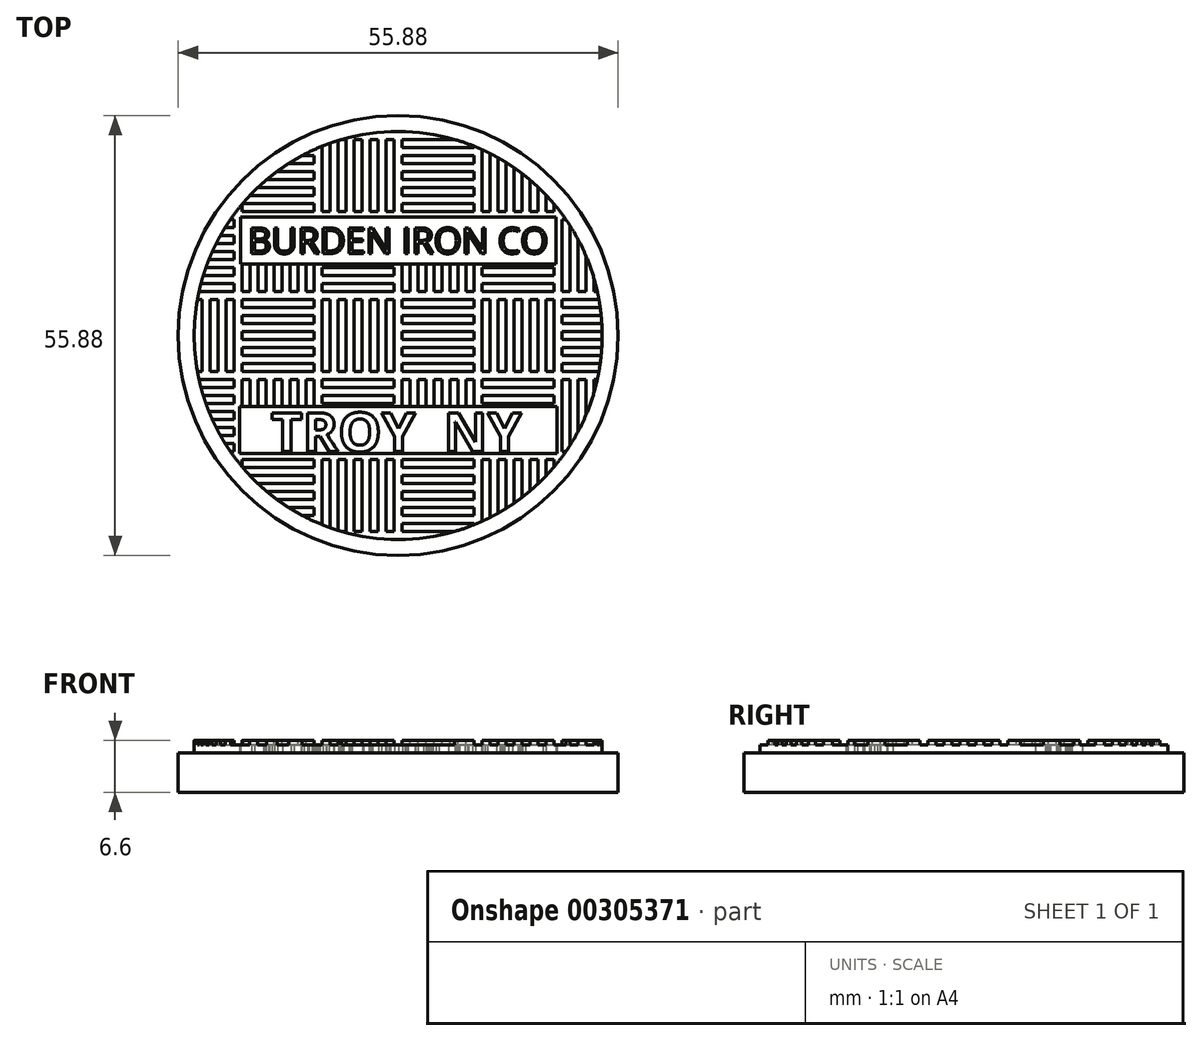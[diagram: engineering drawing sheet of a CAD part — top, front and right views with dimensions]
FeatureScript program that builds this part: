
annotation { "Feature Type Name" : "Feature", "Feature Type Description" : "" }
export const myFeature = defineFeature(function(context is Context, id is Id, definition is map)
    precondition{}
    {
        {
            var Q0;
            Q0=qCreatedBy(makeId("Top.planeOp"),FACE);
            var sketch = newSketch(context, id + "F0", { "sketchPlane" : qUnion([Q0])});
            skCircle(sketch, "E0", {"center": v(0, 0) * mm, "radius": 27.94 * mm});
            skSolve(sketch);
        }
        {
            var Q0;
            Q0 = qSketchRegion(id + "F0", true);
            extrude(context, id + "F1", {"entities" : qUnion([Q0]), "depth" : 6 * mm});
        }
        {
            var Q0;
            Q0=makeQuery(id+"F1.opExtrude","CAP_FACE",FACE,{"disambiguationData":[OSD([sQuery(id+"F0.wireOp",EDGE,"E0")])],"isStart":false});
            var sketch = newSketch(context, id + "F2", { "sketchPlane" : qUnion([Q0])});
            skLineSegment(sketch, "E1.bottom", {"start": v(-9.65, 4.57) * mm, "end": v(-8.64, 4.57) * mm});
            skLineSegment(sketch, "E1.top", {"start": v(-9.65, -4.57) * mm, "end": v(-8.64, -4.57) * mm});
            skLineSegment(sketch, "E1.left", {"start": v(-9.65, 4.57) * mm, "end": v(-9.65, -4.57) * mm});
            skLineSegment(sketch, "E1.right", {"start": v(-8.64, 4.57) * mm, "end": v(-8.64, -4.57) * mm});
            skPoint(sketch, "E2", {"position": v(-9.65, 0) * mm});
            skLineSegment(sketch, "E3.1.0.0", {"start": v(-7.62, 4.57) * mm, "end": v(-7.62, -4.57) * mm});
            skLineSegment(sketch, "E3.1.0.1", {"start": v(-7.62, 4.57) * mm, "end": v(-6.6, 4.57) * mm});
            skLineSegment(sketch, "E3.1.0.2", {"start": v(-6.6, 4.57) * mm, "end": v(-6.6, -4.57) * mm});
            skLineSegment(sketch, "E3.1.0.3", {"start": v(-7.62, -4.57) * mm, "end": v(-6.6, -4.57) * mm});
            skLineSegment(sketch, "E3.2.0.0", {"start": v(-5.59, 4.57) * mm, "end": v(-5.59, -4.57) * mm});
            skLineSegment(sketch, "E3.2.0.1", {"start": v(-5.59, 4.57) * mm, "end": v(-4.57, 4.57) * mm});
            skLineSegment(sketch, "E3.2.0.2", {"start": v(-4.57, 4.57) * mm, "end": v(-4.57, -4.57) * mm});
            skLineSegment(sketch, "E3.2.0.3", {"start": v(-5.59, -4.57) * mm, "end": v(-4.57, -4.57) * mm});
            skLineSegment(sketch, "E3.3.0.0", {"start": v(-3.56, 4.57) * mm, "end": v(-3.56, -4.57) * mm});
            skLineSegment(sketch, "E3.3.0.1", {"start": v(-3.56, 4.57) * mm, "end": v(-2.54, 4.57) * mm});
            skLineSegment(sketch, "E3.3.0.2", {"start": v(-2.54, 4.57) * mm, "end": v(-2.54, -4.57) * mm});
            skLineSegment(sketch, "E3.3.0.3", {"start": v(-3.56, -4.57) * mm, "end": v(-2.54, -4.57) * mm});
            skLineSegment(sketch, "E3.4.0.0", {"start": v(-1.52, 4.57) * mm, "end": v(-1.52, -4.57) * mm});
            skLineSegment(sketch, "E3.4.0.1", {"start": v(-1.52, 4.57) * mm, "end": v(-0.5, 4.57) * mm});
            skLineSegment(sketch, "E3.4.0.2", {"start": v(-0.5, 4.57) * mm, "end": v(-0.5, -4.57) * mm});
            skLineSegment(sketch, "E3.4.0.3", {"start": v(-1.52, -4.57) * mm, "end": v(-0.5, -4.57) * mm});
            skLineSegment(sketch, "E3.direction1", {"start": v(-9.65, -4.57) * mm, "end": v(-7.62, -4.57) * mm, "construction": true});
            skLineSegment(sketch, "E4.bottom", {"start": v(0.5, 4.57) * mm, "end": v(9.65, 4.57) * mm});
            skLineSegment(sketch, "E4.top", {"start": v(0.5, 3.56) * mm, "end": v(9.65, 3.56) * mm});
            skLineSegment(sketch, "E4.left", {"start": v(0.5, 4.57) * mm, "end": v(0.5, 3.56) * mm});
            skLineSegment(sketch, "E4.right", {"start": v(9.65, 4.57) * mm, "end": v(9.65, 3.56) * mm});
            skLineSegment(sketch, "E5.bottom", {"start": v(0.5, 2.54) * mm, "end": v(9.65, 2.54) * mm});
            skLineSegment(sketch, "E5.top", {"start": v(0.5, 1.52) * mm, "end": v(9.65, 1.52) * mm});
            skLineSegment(sketch, "E5.left", {"start": v(0.5, 2.54) * mm, "end": v(0.5, 1.52) * mm});
            skLineSegment(sketch, "E5.right", {"start": v(9.65, 2.54) * mm, "end": v(9.65, 1.52) * mm});
            skPoint(sketch, "E6.firstSnap0", {"position": v(0.5, 2.03) * mm});
            skPoint(sketch, "E6.oppositeSnap0", {"position": v(9.65, 2.03) * mm});
            skLineSegment(sketch, "E6.bottom", {"start": v(0.5, 0.5) * mm, "end": v(9.65, 0.5) * mm});
            skLineSegment(sketch, "E6.top", {"start": v(0.5, -0.5) * mm, "end": v(9.65, -0.5) * mm});
            skLineSegment(sketch, "E6.left", {"start": v(0.5, 0.5) * mm, "end": v(0.5, -0.5) * mm});
            skLineSegment(sketch, "E6.right", {"start": v(9.65, 0.5) * mm, "end": v(9.65, -0.5) * mm});
            skLineSegment(sketch, "E7.bottom", {"start": v(0.5, -1.52) * mm, "end": v(9.65, -1.52) * mm});
            skLineSegment(sketch, "E7.top", {"start": v(0.5, -2.54) * mm, "end": v(9.65, -2.54) * mm});
            skLineSegment(sketch, "E7.left", {"start": v(0.5, -1.52) * mm, "end": v(0.5, -2.54) * mm});
            skLineSegment(sketch, "E7.right", {"start": v(9.65, -1.52) * mm, "end": v(9.65, -2.54) * mm});
            skPoint(sketch, "E8.oppositeSnap0", {"position": v(9.65, -2.03) * mm});
            skLineSegment(sketch, "E8.bottom", {"start": v(0.5, -3.56) * mm, "end": v(9.65, -3.56) * mm});
            skLineSegment(sketch, "E8.top", {"start": v(0.5, -4.57) * mm, "end": v(9.65, -4.57) * mm});
            skLineSegment(sketch, "E8.left", {"start": v(0.5, -3.56) * mm, "end": v(0.5, -4.57) * mm});
            skLineSegment(sketch, "E8.right", {"start": v(9.65, -3.56) * mm, "end": v(9.65, -4.57) * mm});
            skLineSegment(sketch, "E9.bottom", {"start": v(-9.65, 14.73) * mm, "end": v(-0.5, 14.73) * mm});
            skLineSegment(sketch, "E9.top", {"start": v(-9.65, 13.72) * mm, "end": v(-0.5, 13.72) * mm});
            skLineSegment(sketch, "E9.left", {"start": v(-9.65, 14.73) * mm, "end": v(-9.65, 13.72) * mm});
            skLineSegment(sketch, "E9.right", {"start": v(-0.5, 14.73) * mm, "end": v(-0.5, 13.72) * mm});
            skLineSegment(sketch, "E10.bottom", {"start": v(-9.65, 12.7) * mm, "end": v(-0.5, 12.7) * mm});
            skLineSegment(sketch, "E10.top", {"start": v(-9.65, 11.68) * mm, "end": v(-0.5, 11.68) * mm});
            skLineSegment(sketch, "E10.left", {"start": v(-9.65, 12.7) * mm, "end": v(-9.65, 11.68) * mm});
            skLineSegment(sketch, "E10.right", {"start": v(-0.5, 12.7) * mm, "end": v(-0.5, 11.68) * mm});
            skPoint(sketch, "E11.firstSnap0", {"position": v(-9.65, 12.2) * mm});
            skPoint(sketch, "E11.oppositeSnap0", {"position": v(-0.5, 12.2) * mm});
            skLineSegment(sketch, "E11.bottom", {"start": v(-9.65, 10.67) * mm, "end": v(-0.5, 10.67) * mm});
            skLineSegment(sketch, "E11.top", {"start": v(-9.65, 9.65) * mm, "end": v(-0.5, 9.65) * mm});
            skLineSegment(sketch, "E11.left", {"start": v(-9.65, 10.67) * mm, "end": v(-9.65, 9.65) * mm});
            skLineSegment(sketch, "E11.right", {"start": v(-0.5, 10.67) * mm, "end": v(-0.5, 9.65) * mm});
            skLineSegment(sketch, "E12.bottom", {"start": v(-9.65, 8.64) * mm, "end": v(-0.5, 8.64) * mm});
            skLineSegment(sketch, "E12.top", {"start": v(-9.65, 7.62) * mm, "end": v(-0.5, 7.62) * mm});
            skLineSegment(sketch, "E12.left", {"start": v(-9.65, 8.64) * mm, "end": v(-9.65, 7.62) * mm});
            skLineSegment(sketch, "E12.right", {"start": v(-0.5, 8.64) * mm, "end": v(-0.5, 7.62) * mm});
            skPoint(sketch, "E13.oppositeSnap0", {"position": v(-0.5, 8.13) * mm});
            skLineSegment(sketch, "E13.bottom", {"start": v(-9.65, 6.6) * mm, "end": v(-0.5, 6.6) * mm});
            skLineSegment(sketch, "E13.top", {"start": v(-9.65, 5.59) * mm, "end": v(-0.5, 5.59) * mm});
            skLineSegment(sketch, "E13.left", {"start": v(-9.65, 6.6) * mm, "end": v(-9.65, 5.59) * mm});
            skLineSegment(sketch, "E13.right", {"start": v(-0.5, 6.6) * mm, "end": v(-0.5, 5.59) * mm});
            skLineSegment(sketch, "E14.bottom", {"start": v(0.5, 14.73) * mm, "end": v(1.52, 14.73) * mm});
            skLineSegment(sketch, "E14.top", {"start": v(0.5, 5.59) * mm, "end": v(1.52, 5.59) * mm});
            skLineSegment(sketch, "E14.left", {"start": v(0.5, 14.73) * mm, "end": v(0.5, 5.59) * mm});
            skLineSegment(sketch, "E14.right", {"start": v(1.52, 14.73) * mm, "end": v(1.52, 5.59) * mm});
            skPoint(sketch, "E15", {"position": v(0.5, 10.16) * mm});
            skLineSegment(sketch, "E16.1.0.0", {"start": v(2.54, 14.73) * mm, "end": v(2.54, 5.59) * mm});
            skLineSegment(sketch, "E16.1.0.1", {"start": v(2.54, 14.73) * mm, "end": v(3.56, 14.73) * mm});
            skLineSegment(sketch, "E16.1.0.2", {"start": v(3.56, 14.73) * mm, "end": v(3.56, 5.59) * mm});
            skLineSegment(sketch, "E16.1.0.3", {"start": v(2.54, 5.59) * mm, "end": v(3.56, 5.59) * mm});
            skLineSegment(sketch, "E16.2.0.0", {"start": v(4.57, 14.73) * mm, "end": v(4.57, 5.59) * mm});
            skLineSegment(sketch, "E16.2.0.1", {"start": v(4.57, 14.73) * mm, "end": v(5.59, 14.73) * mm});
            skLineSegment(sketch, "E16.2.0.2", {"start": v(5.59, 14.73) * mm, "end": v(5.59, 5.59) * mm});
            skLineSegment(sketch, "E16.2.0.3", {"start": v(4.57, 5.59) * mm, "end": v(5.59, 5.59) * mm});
            skLineSegment(sketch, "E16.3.0.0", {"start": v(6.6, 14.73) * mm, "end": v(6.6, 5.59) * mm});
            skLineSegment(sketch, "E16.3.0.1", {"start": v(6.6, 14.73) * mm, "end": v(7.62, 14.73) * mm});
            skLineSegment(sketch, "E16.3.0.2", {"start": v(7.62, 14.73) * mm, "end": v(7.62, 5.59) * mm});
            skLineSegment(sketch, "E16.3.0.3", {"start": v(6.6, 5.59) * mm, "end": v(7.62, 5.59) * mm});
            skLineSegment(sketch, "E16.4.0.0", {"start": v(8.64, 14.73) * mm, "end": v(8.64, 5.59) * mm});
            skLineSegment(sketch, "E16.4.0.1", {"start": v(8.64, 14.73) * mm, "end": v(9.65, 14.73) * mm});
            skLineSegment(sketch, "E16.4.0.2", {"start": v(9.65, 14.73) * mm, "end": v(9.65, 5.59) * mm});
            skLineSegment(sketch, "E16.4.0.3", {"start": v(8.64, 5.59) * mm, "end": v(9.65, 5.59) * mm});
            skLineSegment(sketch, "E16.direction1", {"start": v(0.5, 5.59) * mm, "end": v(2.54, 5.59) * mm, "construction": true});
            skLineSegment(sketch, "E17.1.0.0", {"start": v(20.83, -1.52) * mm, "end": v(29.97, -1.52) * mm});
            skLineSegment(sketch, "E17.1.0.1", {"start": v(10.67, 14.73) * mm, "end": v(19.81, 14.73) * mm});
            skLineSegment(sketch, "E17.1.0.2", {"start": v(10.67, 9.65) * mm, "end": v(19.81, 9.65) * mm});
            skPoint(sketch, "E17.1.0.3", {"position": v(10.67, 0) * mm});
            skLineSegment(sketch, "E17.1.0.4", {"start": v(19.81, 4.57) * mm, "end": v(19.81, -4.57) * mm});
            skPoint(sketch, "E17.1.0.5", {"position": v(10.67, 12.2) * mm});
            skLineSegment(sketch, "E17.1.0.6", {"start": v(10.67, 5.59) * mm, "end": v(19.81, 5.59) * mm});
            skLineSegment(sketch, "E17.1.0.7", {"start": v(16.76, 4.57) * mm, "end": v(16.76, -4.57) * mm});
            skLineSegment(sketch, "E17.1.0.8", {"start": v(23.88, 14.73) * mm, "end": v(23.88, 5.59) * mm});
            skLineSegment(sketch, "E17.1.0.9", {"start": v(10.67, 12.7) * mm, "end": v(19.81, 12.7) * mm});
            skLineSegment(sketch, "E17.1.0.10", {"start": v(25.9, 14.73) * mm, "end": v(25.9, 5.59) * mm});
            skLineSegment(sketch, "E17.1.0.11", {"start": v(21.84, 14.73) * mm, "end": v(21.84, 5.59) * mm});
            skLineSegment(sketch, "E17.1.0.12", {"start": v(22.86, 14.73) * mm, "end": v(22.86, 5.59) * mm});
            skLineSegment(sketch, "E17.1.0.13", {"start": v(20.83, -2.54) * mm, "end": v(29.97, -2.54) * mm});
            skLineSegment(sketch, "E17.1.0.14", {"start": v(10.67, 6.6) * mm, "end": v(19.81, 6.6) * mm});
            skLineSegment(sketch, "E17.1.0.15", {"start": v(26.92, 14.73) * mm, "end": v(26.92, 5.59) * mm});
            skLineSegment(sketch, "E17.1.0.16", {"start": v(10.67, 13.72) * mm, "end": v(19.81, 13.72) * mm});
            skLineSegment(sketch, "E17.1.0.17", {"start": v(20.83, 1.52) * mm, "end": v(29.97, 1.52) * mm});
            skLineSegment(sketch, "E17.1.0.18", {"start": v(24.9, 14.73) * mm, "end": v(24.9, 5.59) * mm});
            skLineSegment(sketch, "E17.1.0.19", {"start": v(10.67, 8.64) * mm, "end": v(19.81, 8.64) * mm});
            skLineSegment(sketch, "E17.1.0.20", {"start": v(10.67, 11.68) * mm, "end": v(19.81, 11.68) * mm});
            skPoint(sketch, "E17.1.0.21", {"position": v(20.83, 10.16) * mm});
            skLineSegment(sketch, "E17.1.0.22", {"start": v(17.78, 4.57) * mm, "end": v(17.78, -4.57) * mm});
            skLineSegment(sketch, "E17.1.0.23", {"start": v(20.83, 0.5) * mm, "end": v(29.97, 0.5) * mm});
            skLineSegment(sketch, "E17.1.0.24", {"start": v(20.83, -4.57) * mm, "end": v(29.97, -4.57) * mm});
            skLineSegment(sketch, "E17.1.0.25", {"start": v(10.67, 10.67) * mm, "end": v(19.81, 10.67) * mm});
            skLineSegment(sketch, "E17.1.0.26", {"start": v(29.97, 14.73) * mm, "end": v(29.97, 5.59) * mm});
            skLineSegment(sketch, "E17.1.0.27", {"start": v(10.67, 7.62) * mm, "end": v(19.81, 7.62) * mm});
            skLineSegment(sketch, "E17.1.0.28", {"start": v(18.8, 4.57) * mm, "end": v(18.8, -4.57) * mm});
            skLineSegment(sketch, "E17.1.0.29", {"start": v(15.75, 4.57) * mm, "end": v(15.75, -4.57) * mm});
            skLineSegment(sketch, "E17.1.0.30", {"start": v(14.73, 4.57) * mm, "end": v(14.73, -4.57) * mm});
            skLineSegment(sketch, "E17.1.0.31", {"start": v(13.72, 4.57) * mm, "end": v(13.72, -4.57) * mm});
            skLineSegment(sketch, "E17.1.0.32", {"start": v(28.96, 14.73) * mm, "end": v(28.96, 5.59) * mm});
            skLineSegment(sketch, "E17.1.0.33", {"start": v(12.7, 4.57) * mm, "end": v(12.7, -4.57) * mm});
            skLineSegment(sketch, "E17.1.0.34", {"start": v(11.68, 4.57) * mm, "end": v(11.68, -4.57) * mm});
            skLineSegment(sketch, "E17.1.0.35", {"start": v(10.67, 4.57) * mm, "end": v(10.67, -4.57) * mm});
            skLineSegment(sketch, "E17.1.0.36", {"start": v(20.83, -0.5) * mm, "end": v(29.97, -0.5) * mm});
            skLineSegment(sketch, "E17.1.0.37", {"start": v(20.83, -3.56) * mm, "end": v(29.97, -3.56) * mm});
            skLineSegment(sketch, "E17.1.0.38", {"start": v(27.94, 14.73) * mm, "end": v(27.94, 5.59) * mm});
            skPoint(sketch, "E17.1.0.39", {"position": v(19.81, 12.2) * mm});
            skLineSegment(sketch, "E17.1.0.40", {"start": v(20.83, 2.54) * mm, "end": v(29.97, 2.54) * mm});
            skPoint(sketch, "E17.1.0.41", {"position": v(19.81, 8.13) * mm});
            skPoint(sketch, "E17.1.0.42", {"position": v(29.97, -2.03) * mm});
            skPoint(sketch, "E17.1.0.43", {"position": v(29.97, 2.03) * mm});
            skLineSegment(sketch, "E17.1.0.44", {"start": v(20.83, 14.73) * mm, "end": v(20.83, 5.59) * mm});
            skLineSegment(sketch, "E17.1.0.45", {"start": v(20.83, 3.56) * mm, "end": v(29.97, 3.56) * mm});
            skLineSegment(sketch, "E17.1.0.46", {"start": v(20.83, 4.57) * mm, "end": v(29.97, 4.57) * mm});
            skPoint(sketch, "E17.1.0.47", {"position": v(20.83, 2.03) * mm});
            skLineSegment(sketch, "E17.1.0.48", {"start": v(10.67, 10.67) * mm, "end": v(10.67, 9.65) * mm});
            skLineSegment(sketch, "E17.1.0.49", {"start": v(18.8, 4.57) * mm, "end": v(19.81, 4.57) * mm});
            skLineSegment(sketch, "E17.1.0.50", {"start": v(10.67, -4.57) * mm, "end": v(12.7, -4.57) * mm, "construction": true});
            skLineSegment(sketch, "E17.1.0.51", {"start": v(18.8, -4.57) * mm, "end": v(19.81, -4.57) * mm});
            skLineSegment(sketch, "E17.1.0.52", {"start": v(28.96, 5.59) * mm, "end": v(29.97, 5.59) * mm});
            skLineSegment(sketch, "E17.1.0.53", {"start": v(26.92, 14.73) * mm, "end": v(27.94, 14.73) * mm});
            skLineSegment(sketch, "E17.1.0.54", {"start": v(20.83, 5.59) * mm, "end": v(22.86, 5.59) * mm, "construction": true});
            skLineSegment(sketch, "E17.1.0.55", {"start": v(22.86, 14.73) * mm, "end": v(23.88, 14.73) * mm});
            skLineSegment(sketch, "E17.1.0.56", {"start": v(20.83, -3.56) * mm, "end": v(20.83, -4.57) * mm});
            skLineSegment(sketch, "E17.1.0.57", {"start": v(10.67, 8.64) * mm, "end": v(10.67, 7.62) * mm});
            skLineSegment(sketch, "E17.1.0.58", {"start": v(14.73, -4.57) * mm, "end": v(15.75, -4.57) * mm});
            skLineSegment(sketch, "E17.1.0.59", {"start": v(10.67, 14.73) * mm, "end": v(10.67, 13.72) * mm});
            skLineSegment(sketch, "E17.1.0.60", {"start": v(20.83, -1.52) * mm, "end": v(20.83, -2.54) * mm});
            skLineSegment(sketch, "E17.1.0.61", {"start": v(28.96, 14.73) * mm, "end": v(29.97, 14.73) * mm});
            skLineSegment(sketch, "E17.1.0.62", {"start": v(20.83, 5.59) * mm, "end": v(21.84, 5.59) * mm});
            skLineSegment(sketch, "E17.1.0.63", {"start": v(16.76, -4.57) * mm, "end": v(17.78, -4.57) * mm});
            skLineSegment(sketch, "E17.1.0.64", {"start": v(20.83, 0.5) * mm, "end": v(20.83, -0.5) * mm});
            skLineSegment(sketch, "E17.1.0.65", {"start": v(24.9, 14.73) * mm, "end": v(25.9, 14.73) * mm});
            skLineSegment(sketch, "E17.1.0.66", {"start": v(29.97, -3.56) * mm, "end": v(29.97, -4.57) * mm});
            skLineSegment(sketch, "E17.1.0.67", {"start": v(12.7, -4.57) * mm, "end": v(13.72, -4.57) * mm});
            skLineSegment(sketch, "E17.1.0.68", {"start": v(12.7, 4.57) * mm, "end": v(13.72, 4.57) * mm});
            skLineSegment(sketch, "E17.1.0.69", {"start": v(20.83, 14.73) * mm, "end": v(21.84, 14.73) * mm});
            skLineSegment(sketch, "E17.1.0.70", {"start": v(20.83, 4.57) * mm, "end": v(20.83, 3.56) * mm});
            skLineSegment(sketch, "E17.1.0.71", {"start": v(10.67, -4.57) * mm, "end": v(11.68, -4.57) * mm});
            skLineSegment(sketch, "E17.1.0.72", {"start": v(10.67, 4.57) * mm, "end": v(11.68, 4.57) * mm});
            skLineSegment(sketch, "E17.1.0.73", {"start": v(19.81, 14.73) * mm, "end": v(19.81, 13.72) * mm});
            skLineSegment(sketch, "E17.1.0.74", {"start": v(10.67, 6.6) * mm, "end": v(10.67, 5.59) * mm});
            skLineSegment(sketch, "E17.1.0.75", {"start": v(19.81, 8.64) * mm, "end": v(19.81, 7.62) * mm});
            skLineSegment(sketch, "E17.1.0.76", {"start": v(19.81, 12.7) * mm, "end": v(19.81, 11.68) * mm});
            skLineSegment(sketch, "E17.1.0.77", {"start": v(24.9, 5.59) * mm, "end": v(25.9, 5.59) * mm});
            skLineSegment(sketch, "E17.1.0.78", {"start": v(22.86, 5.59) * mm, "end": v(23.88, 5.59) * mm});
            skLineSegment(sketch, "E17.1.0.79", {"start": v(10.67, 12.7) * mm, "end": v(10.67, 11.68) * mm});
            skLineSegment(sketch, "E17.1.0.80", {"start": v(20.83, 2.54) * mm, "end": v(20.83, 1.52) * mm});
            skLineSegment(sketch, "E17.1.0.81", {"start": v(19.81, 10.67) * mm, "end": v(19.81, 9.65) * mm});
            skLineSegment(sketch, "E17.1.0.82", {"start": v(29.97, -1.52) * mm, "end": v(29.97, -2.54) * mm});
            skLineSegment(sketch, "E17.1.0.83", {"start": v(16.76, 4.57) * mm, "end": v(17.78, 4.57) * mm});
            skLineSegment(sketch, "E17.1.0.84", {"start": v(29.97, 4.57) * mm, "end": v(29.97, 3.56) * mm});
            skLineSegment(sketch, "E17.1.0.85", {"start": v(29.97, 0.5) * mm, "end": v(29.97, -0.5) * mm});
            skLineSegment(sketch, "E17.1.0.86", {"start": v(14.73, 4.57) * mm, "end": v(15.75, 4.57) * mm});
            skLineSegment(sketch, "E17.1.0.87", {"start": v(19.81, 6.6) * mm, "end": v(19.81, 5.59) * mm});
            skLineSegment(sketch, "E17.1.0.88", {"start": v(26.92, 5.59) * mm, "end": v(27.94, 5.59) * mm});
            skLineSegment(sketch, "E17.1.0.89", {"start": v(29.97, 2.54) * mm, "end": v(29.97, 1.52) * mm});
            skLineSegment(sketch, "E17.direction1", {"start": v(-9.65, -4.57) * mm, "end": v(10.67, -4.57) * mm, "construction": true});
            skLineSegment(sketch, "E18.1.0.0", {"start": v(-29.97, 8.64) * mm, "end": v(-20.83, 8.64) * mm});
            skLineSegment(sketch, "E18.1.0.1", {"start": v(-15.75, 14.73) * mm, "end": v(-15.75, 5.59) * mm});
            skLineSegment(sketch, "E18.1.0.2", {"start": v(-19.81, 4.57) * mm, "end": v(-10.67, 4.57) * mm});
            skLineSegment(sketch, "E18.1.0.3", {"start": v(-19.81, -3.56) * mm, "end": v(-10.67, -3.56) * mm});
            skLineSegment(sketch, "E18.1.0.4", {"start": v(-19.81, 1.52) * mm, "end": v(-10.67, 1.52) * mm});
            skLineSegment(sketch, "E18.1.0.5", {"start": v(-29.97, 13.72) * mm, "end": v(-20.83, 13.72) * mm});
            skLineSegment(sketch, "E18.1.0.6", {"start": v(-29.97, 5.59) * mm, "end": v(-20.83, 5.59) * mm});
            skPoint(sketch, "E18.1.0.7", {"position": v(-29.97, 0) * mm});
            skLineSegment(sketch, "E18.1.0.8", {"start": v(-19.81, 2.54) * mm, "end": v(-10.67, 2.54) * mm});
            skLineSegment(sketch, "E18.1.0.9", {"start": v(-29.97, 14.73) * mm, "end": v(-20.83, 14.73) * mm});
            skLineSegment(sketch, "E18.1.0.10", {"start": v(-29.97, 6.6) * mm, "end": v(-20.83, 6.6) * mm});
            skLineSegment(sketch, "E18.1.0.11", {"start": v(-13.72, 14.73) * mm, "end": v(-13.72, 5.59) * mm});
            skLineSegment(sketch, "E18.1.0.12", {"start": v(-16.76, 14.73) * mm, "end": v(-16.76, 5.59) * mm});
            skLineSegment(sketch, "E18.1.0.14", {"start": v(-29.97, 9.65) * mm, "end": v(-20.83, 9.65) * mm});
            skLineSegment(sketch, "E18.1.0.15", {"start": v(-20.83, 4.57) * mm, "end": v(-20.83, -4.57) * mm});
            skLineSegment(sketch, "E18.1.0.16", {"start": v(-19.81, -2.54) * mm, "end": v(-10.67, -2.54) * mm});
            skLineSegment(sketch, "E18.1.0.18", {"start": v(-29.97, 10.67) * mm, "end": v(-20.83, 10.67) * mm});
            skLineSegment(sketch, "E18.1.0.19", {"start": v(-17.78, 14.73) * mm, "end": v(-17.78, 5.59) * mm});
            skLineSegment(sketch, "E18.1.0.20", {"start": v(-19.81, -1.52) * mm, "end": v(-10.67, -1.52) * mm});
            skPoint(sketch, "E18.1.0.21", {"position": v(-19.81, 10.16) * mm});
            skLineSegment(sketch, "E18.1.0.22", {"start": v(-21.84, 4.57) * mm, "end": v(-21.84, -4.57) * mm});
            skLineSegment(sketch, "E18.1.0.23", {"start": v(-18.8, 14.73) * mm, "end": v(-18.8, 5.59) * mm});
            skLineSegment(sketch, "E18.1.0.24", {"start": v(-23.88, 4.57) * mm, "end": v(-23.88, -4.57) * mm});
            skLineSegment(sketch, "E18.1.0.25", {"start": v(-24.9, 4.57) * mm, "end": v(-24.9, -4.57) * mm});
            skLineSegment(sketch, "E18.1.0.26", {"start": v(-25.9, 4.57) * mm, "end": v(-25.9, -4.57) * mm});
            skLineSegment(sketch, "E18.1.0.27", {"start": v(-10.67, 14.73) * mm, "end": v(-10.67, 5.59) * mm});
            skLineSegment(sketch, "E18.1.0.28", {"start": v(-26.92, 4.57) * mm, "end": v(-26.92, -4.57) * mm});
            skLineSegment(sketch, "E18.1.0.29", {"start": v(-27.94, 4.57) * mm, "end": v(-27.94, -4.57) * mm});
            skLineSegment(sketch, "E18.1.0.30", {"start": v(-28.96, 4.57) * mm, "end": v(-28.96, -4.57) * mm});
            skLineSegment(sketch, "E18.1.0.31", {"start": v(-29.97, 4.57) * mm, "end": v(-29.97, -4.57) * mm});
            skLineSegment(sketch, "E18.1.0.32", {"start": v(-22.86, 4.57) * mm, "end": v(-22.86, -4.57) * mm});
            skPoint(sketch, "E18.1.0.33", {"position": v(-10.67, 2.03) * mm});
            skLineSegment(sketch, "E18.1.0.34", {"start": v(-29.97, 11.68) * mm, "end": v(-20.83, 11.68) * mm});
            skLineSegment(sketch, "E18.1.0.35", {"start": v(-14.73, 14.73) * mm, "end": v(-14.73, 5.59) * mm});
            skLineSegment(sketch, "E18.1.0.36", {"start": v(-19.81, -0.5) * mm, "end": v(-10.67, -0.5) * mm});
            skPoint(sketch, "E18.1.0.37", {"position": v(-29.97, 12.2) * mm});
            skLineSegment(sketch, "E18.1.0.38", {"start": v(-29.97, 12.7) * mm, "end": v(-20.83, 12.7) * mm});
            skLineSegment(sketch, "E18.1.0.39", {"start": v(-11.68, 14.73) * mm, "end": v(-11.68, 5.59) * mm});
            skLineSegment(sketch, "E18.1.0.40", {"start": v(-19.81, 0.5) * mm, "end": v(-10.67, 0.5) * mm});
            skLineSegment(sketch, "E18.1.0.41", {"start": v(-12.7, 14.73) * mm, "end": v(-12.7, 5.59) * mm});
            skLineSegment(sketch, "E18.1.0.42", {"start": v(-29.97, 7.62) * mm, "end": v(-20.83, 7.62) * mm});
            skPoint(sketch, "E18.1.0.43", {"position": v(-10.67, -2.03) * mm});
            skLineSegment(sketch, "E18.1.0.44", {"start": v(-19.81, 3.56) * mm, "end": v(-10.67, 3.56) * mm});
            skLineSegment(sketch, "E18.1.0.45", {"start": v(-19.81, -4.57) * mm, "end": v(-10.67, -4.57) * mm});
            skPoint(sketch, "E18.1.0.46", {"position": v(-20.83, 8.13) * mm});
            skLineSegment(sketch, "E18.1.0.47", {"start": v(-19.81, 14.73) * mm, "end": v(-19.81, 5.59) * mm});
            skPoint(sketch, "E18.1.0.48", {"position": v(-20.83, 12.2) * mm});
            skPoint(sketch, "E18.1.0.49", {"position": v(-19.81, 2.03) * mm});
            skLineSegment(sketch, "E18.1.0.50", {"start": v(-13.72, 14.73) * mm, "end": v(-12.7, 14.73) * mm});
            skLineSegment(sketch, "E18.1.0.51", {"start": v(-17.78, 5.59) * mm, "end": v(-16.76, 5.59) * mm});
            skLineSegment(sketch, "E18.1.0.52", {"start": v(-29.97, -4.57) * mm, "end": v(-27.94, -4.57) * mm, "construction": true});
            skLineSegment(sketch, "E18.1.0.53", {"start": v(-10.67, -1.52) * mm, "end": v(-10.67, -2.54) * mm});
            skLineSegment(sketch, "E18.1.0.54", {"start": v(-29.97, 10.67) * mm, "end": v(-29.97, 9.65) * mm});
            skLineSegment(sketch, "E18.1.0.55", {"start": v(-21.84, -4.57) * mm, "end": v(-20.83, -4.57) * mm});
            skLineSegment(sketch, "E18.1.0.56", {"start": v(-19.81, -1.52) * mm, "end": v(-19.81, -2.54) * mm});
            skLineSegment(sketch, "E18.1.0.57", {"start": v(-17.78, 14.73) * mm, "end": v(-16.76, 14.73) * mm});
            skLineSegment(sketch, "E18.1.0.58", {"start": v(-10.67, 4.57) * mm, "end": v(-10.67, 3.56) * mm});
            skLineSegment(sketch, "E18.1.0.59", {"start": v(-10.67, -3.56) * mm, "end": v(-10.67, -4.57) * mm});
            skLineSegment(sketch, "E18.1.0.60", {"start": v(-19.81, 5.59) * mm, "end": v(-17.78, 5.59) * mm, "construction": true});
            skLineSegment(sketch, "E18.1.0.61", {"start": v(-21.84, 4.57) * mm, "end": v(-20.83, 4.57) * mm});
            skLineSegment(sketch, "E18.1.0.62", {"start": v(-10.67, 0.5) * mm, "end": v(-10.67, -0.5) * mm});
            skLineSegment(sketch, "E18.1.0.63", {"start": v(-11.68, 5.59) * mm, "end": v(-10.67, 5.59) * mm});
            skLineSegment(sketch, "E18.1.0.64", {"start": v(-25.9, -4.57) * mm, "end": v(-24.9, -4.57) * mm});
            skLineSegment(sketch, "E18.1.0.65", {"start": v(-29.97, 12.7) * mm, "end": v(-29.97, 11.68) * mm});
            skLineSegment(sketch, "E18.1.0.66", {"start": v(-27.94, -4.57) * mm, "end": v(-26.92, -4.57) * mm});
            skLineSegment(sketch, "E18.1.0.67", {"start": v(-19.81, 0.5) * mm, "end": v(-19.81, -0.5) * mm});
            skLineSegment(sketch, "E18.1.0.68", {"start": v(-27.94, 4.57) * mm, "end": v(-26.92, 4.57) * mm});
            skLineSegment(sketch, "E18.1.0.69", {"start": v(-29.97, -4.57) * mm, "end": v(-28.96, -4.57) * mm});
            skLineSegment(sketch, "E18.1.0.70", {"start": v(-29.97, 4.57) * mm, "end": v(-28.96, 4.57) * mm});
            skLineSegment(sketch, "E18.1.0.71", {"start": v(-23.88, -4.57) * mm, "end": v(-22.86, -4.57) * mm});
            skLineSegment(sketch, "E18.1.0.72", {"start": v(-19.81, 5.59) * mm, "end": v(-18.8, 5.59) * mm});
            skLineSegment(sketch, "E18.1.0.73", {"start": v(-11.68, 14.73) * mm, "end": v(-10.67, 14.73) * mm});
            skLineSegment(sketch, "E18.1.0.74", {"start": v(-19.81, 4.57) * mm, "end": v(-19.81, 3.56) * mm});
            skLineSegment(sketch, "E18.1.0.75", {"start": v(-19.81, -3.56) * mm, "end": v(-19.81, -4.57) * mm});
            skLineSegment(sketch, "E18.1.0.76", {"start": v(-29.97, 8.64) * mm, "end": v(-29.97, 7.62) * mm});
            skLineSegment(sketch, "E18.1.0.77", {"start": v(-10.67, 2.54) * mm, "end": v(-10.67, 1.52) * mm});
            skLineSegment(sketch, "E18.1.0.78", {"start": v(-20.83, 14.73) * mm, "end": v(-20.83, 13.72) * mm});
            skLineSegment(sketch, "E18.1.0.79", {"start": v(-20.83, 6.6) * mm, "end": v(-20.83, 5.59) * mm});
            skLineSegment(sketch, "E18.1.0.80", {"start": v(-13.72, 5.59) * mm, "end": v(-12.7, 5.59) * mm});
            skLineSegment(sketch, "E18.1.0.81", {"start": v(-19.81, 14.73) * mm, "end": v(-18.8, 14.73) * mm});
            skLineSegment(sketch, "E18.1.0.82", {"start": v(-29.97, 14.73) * mm, "end": v(-29.97, 13.72) * mm});
            skLineSegment(sketch, "E18.1.0.83", {"start": v(-29.97, 6.6) * mm, "end": v(-29.97, 5.59) * mm});
            skLineSegment(sketch, "E18.1.0.84", {"start": v(-15.75, 14.73) * mm, "end": v(-14.73, 14.73) * mm});
            skLineSegment(sketch, "E18.1.0.85", {"start": v(-20.83, 10.67) * mm, "end": v(-20.83, 9.65) * mm});
            skLineSegment(sketch, "E18.1.0.86", {"start": v(-20.83, 8.64) * mm, "end": v(-20.83, 7.62) * mm});
            skLineSegment(sketch, "E18.1.0.87", {"start": v(-15.75, 5.59) * mm, "end": v(-14.73, 5.59) * mm});
            skLineSegment(sketch, "E18.1.0.88", {"start": v(-20.83, 12.7) * mm, "end": v(-20.83, 11.68) * mm});
            skLineSegment(sketch, "E18.1.0.89", {"start": v(-25.9, 4.57) * mm, "end": v(-24.9, 4.57) * mm});
            skLineSegment(sketch, "E18.1.0.90", {"start": v(-23.88, 4.57) * mm, "end": v(-22.86, 4.57) * mm});
            skLineSegment(sketch, "E18.1.0.91", {"start": v(-19.81, 2.54) * mm, "end": v(-19.81, 1.52) * mm});
            skLineSegment(sketch, "E18.direction1", {"start": v(-9.65, -4.57) * mm, "end": v(-29.97, -4.57) * mm, "construction": true});
            skLineSegment(sketch, "E19.0.1.0", {"start": v(10.67, 28.96) * mm, "end": v(19.81, 28.96) * mm});
            skLineSegment(sketch, "E19.0.1.1", {"start": v(10.67, 35.05) * mm, "end": v(19.81, 35.05) * mm});
            skLineSegment(sketch, "E19.0.1.2", {"start": v(3.56, 35.05) * mm, "end": v(3.56, 25.9) * mm});
            skPoint(sketch, "E19.0.1.3", {"position": v(-19.81, 30.48) * mm});
            skLineSegment(sketch, "E19.0.1.4", {"start": v(20.83, 19.81) * mm, "end": v(29.97, 19.81) * mm});
            skLineSegment(sketch, "E19.0.1.5", {"start": v(-14.73, 35.05) * mm, "end": v(-14.73, 25.9) * mm});
            skLineSegment(sketch, "E19.0.1.6", {"start": v(-19.81, 17.78) * mm, "end": v(-10.67, 17.78) * mm});
            skLineSegment(sketch, "E19.0.1.7", {"start": v(-1.52, 24.9) * mm, "end": v(-1.52, 15.75) * mm});
            skLineSegment(sketch, "E19.0.1.8", {"start": v(-3.56, 24.9) * mm, "end": v(-3.56, 15.75) * mm});
            skLineSegment(sketch, "E19.0.1.9", {"start": v(11.68, 24.9) * mm, "end": v(11.68, 15.75) * mm});
            skLineSegment(sketch, "E19.0.1.10", {"start": v(-22.86, 24.9) * mm, "end": v(-22.86, 15.75) * mm});
            skLineSegment(sketch, "E19.0.1.11", {"start": v(-4.57, 24.9) * mm, "end": v(-4.57, 15.75) * mm});
            skLineSegment(sketch, "E19.0.1.12", {"start": v(-5.59, 24.9) * mm, "end": v(-5.59, 15.75) * mm});
            skLineSegment(sketch, "E19.0.1.13", {"start": v(-6.6, 24.9) * mm, "end": v(-6.6, 15.75) * mm});
            skLineSegment(sketch, "E19.0.1.14", {"start": v(-29.97, 29.97) * mm, "end": v(-20.83, 29.97) * mm});
            skLineSegment(sketch, "E19.0.1.15", {"start": v(-7.62, 24.9) * mm, "end": v(-7.62, 15.75) * mm});
            skLineSegment(sketch, "E19.0.1.16", {"start": v(-8.64, 24.9) * mm, "end": v(-8.64, 15.75) * mm});
            skLineSegment(sketch, "E19.0.1.17", {"start": v(10.67, 32) * mm, "end": v(19.81, 32) * mm});
            skLineSegment(sketch, "E19.0.1.18", {"start": v(-9.65, 24.9) * mm, "end": v(-9.65, 15.75) * mm});
            skPoint(sketch, "E19.0.1.19", {"position": v(-9.65, 32.51) * mm});
            skLineSegment(sketch, "E19.0.1.20", {"start": v(10.67, 29.97) * mm, "end": v(19.81, 29.97) * mm});
            skLineSegment(sketch, "E19.0.1.21", {"start": v(0.5, 18.8) * mm, "end": v(9.65, 18.8) * mm});
            skLineSegment(sketch, "E19.0.1.22", {"start": v(20.83, 21.84) * mm, "end": v(29.97, 21.84) * mm});
            skLineSegment(sketch, "E19.0.1.23", {"start": v(-9.65, 15.75) * mm, "end": v(10.67, 15.75) * mm, "construction": true});
            skLineSegment(sketch, "E19.0.1.24", {"start": v(-2.54, 24.9) * mm, "end": v(-2.54, 15.75) * mm});
            skLineSegment(sketch, "E19.0.1.25", {"start": v(20.83, 16.76) * mm, "end": v(29.97, 16.76) * mm});
            skLineSegment(sketch, "E19.0.1.26", {"start": v(-19.81, 19.81) * mm, "end": v(-10.67, 19.81) * mm});
            skLineSegment(sketch, "E19.0.1.27", {"start": v(-29.97, 30.99) * mm, "end": v(-20.83, 30.99) * mm});
            skLineSegment(sketch, "E19.0.1.28", {"start": v(2.54, 35.05) * mm, "end": v(2.54, 25.9) * mm});
            skLineSegment(sketch, "E19.0.1.29", {"start": v(-9.65, 30.99) * mm, "end": v(-0.5, 30.99) * mm});
            skLineSegment(sketch, "E19.0.1.30", {"start": v(-19.81, 22.86) * mm, "end": v(-10.67, 22.86) * mm});
            skLineSegment(sketch, "E19.0.1.31", {"start": v(-10.67, 35.05) * mm, "end": v(-10.67, 25.9) * mm});
            skLineSegment(sketch, "E19.0.1.32", {"start": v(-19.81, 35.05) * mm, "end": v(-19.81, 25.9) * mm});
            skLineSegment(sketch, "E19.0.1.33", {"start": v(22.86, 35.05) * mm, "end": v(22.86, 25.9) * mm});
            skLineSegment(sketch, "E19.0.1.34", {"start": v(15.75, 24.9) * mm, "end": v(15.75, 15.75) * mm});
            skLineSegment(sketch, "E19.0.1.35", {"start": v(0.5, 16.76) * mm, "end": v(9.65, 16.76) * mm});
            skPoint(sketch, "E19.0.1.36", {"position": v(19.81, 28.45) * mm});
            skLineSegment(sketch, "E19.0.1.37", {"start": v(0.5, 24.9) * mm, "end": v(9.65, 24.9) * mm});
            skLineSegment(sketch, "E19.0.1.38", {"start": v(17.78, 24.9) * mm, "end": v(17.78, 15.75) * mm});
            skLineSegment(sketch, "E19.0.1.39", {"start": v(19.81, 24.9) * mm, "end": v(19.81, 15.75) * mm});
            skLineSegment(sketch, "E19.0.1.40", {"start": v(4.57, 35.05) * mm, "end": v(4.57, 25.9) * mm});
            skLineSegment(sketch, "E19.0.1.41", {"start": v(-9.65, 28.96) * mm, "end": v(-0.5, 28.96) * mm});
            skLineSegment(sketch, "E19.0.1.42", {"start": v(-29.97, 28.96) * mm, "end": v(-20.83, 28.96) * mm});
            skLineSegment(sketch, "E19.0.1.43", {"start": v(27.94, 35.05) * mm, "end": v(27.94, 25.9) * mm});
            skPoint(sketch, "E19.0.1.44", {"position": v(-29.97, 32.51) * mm});
            skLineSegment(sketch, "E19.0.1.45", {"start": v(-29.97, 25.9) * mm, "end": v(-20.83, 25.9) * mm});
            skLineSegment(sketch, "E19.0.1.46", {"start": v(-25.9, 24.9) * mm, "end": v(-25.9, 15.75) * mm});
            skLineSegment(sketch, "E19.0.1.47", {"start": v(21.84, 35.05) * mm, "end": v(21.84, 25.9) * mm});
            skLineSegment(sketch, "E19.0.1.48", {"start": v(-29.97, 33.02) * mm, "end": v(-20.83, 33.02) * mm});
            skLineSegment(sketch, "E19.0.1.49", {"start": v(-17.78, 35.05) * mm, "end": v(-17.78, 25.9) * mm});
            skLineSegment(sketch, "E19.0.1.50", {"start": v(18.8, 24.9) * mm, "end": v(18.8, 15.75) * mm});
            skPoint(sketch, "E19.0.1.51", {"position": v(19.81, 32.51) * mm});
            skLineSegment(sketch, "E19.0.1.52", {"start": v(7.62, 35.05) * mm, "end": v(7.62, 25.9) * mm});
            skLineSegment(sketch, "E19.0.1.53", {"start": v(-29.97, 34.04) * mm, "end": v(-20.83, 34.04) * mm});
            skLineSegment(sketch, "E19.0.1.54", {"start": v(-24.9, 24.9) * mm, "end": v(-24.9, 15.75) * mm});
            skLineSegment(sketch, "E19.0.1.55", {"start": v(25.9, 35.05) * mm, "end": v(25.9, 25.9) * mm});
            skLineSegment(sketch, "E19.0.1.56", {"start": v(-19.81, 23.88) * mm, "end": v(-10.67, 23.88) * mm});
            skLineSegment(sketch, "E19.0.1.57", {"start": v(10.67, 27.94) * mm, "end": v(19.81, 27.94) * mm});
            skPoint(sketch, "E19.0.1.58", {"position": v(20.83, 30.48) * mm});
            skLineSegment(sketch, "E19.0.1.59", {"start": v(0.5, 21.84) * mm, "end": v(9.65, 21.84) * mm});
            skLineSegment(sketch, "E19.0.1.60", {"start": v(-9.65, 34.04) * mm, "end": v(-0.5, 34.04) * mm});
            skLineSegment(sketch, "E19.0.1.61", {"start": v(-9.65, 25.9) * mm, "end": v(-0.5, 25.9) * mm});
            skLineSegment(sketch, "E19.0.1.62", {"start": v(0.5, 23.88) * mm, "end": v(9.65, 23.88) * mm});
            skLineSegment(sketch, "E19.0.1.63", {"start": v(20.83, 20.83) * mm, "end": v(29.97, 20.83) * mm});
            skLineSegment(sketch, "E19.0.1.64", {"start": v(10.67, 25.9) * mm, "end": v(19.81, 25.9) * mm});
            skLineSegment(sketch, "E19.0.1.65", {"start": v(-9.65, 27.94) * mm, "end": v(-0.5, 27.94) * mm});
            skLineSegment(sketch, "E19.0.1.66", {"start": v(-15.75, 35.05) * mm, "end": v(-15.75, 25.9) * mm});
            skPoint(sketch, "E19.0.1.67", {"position": v(-10.67, 18.29) * mm});
            skLineSegment(sketch, "E19.0.1.68", {"start": v(20.83, 22.86) * mm, "end": v(29.97, 22.86) * mm});
            skLineSegment(sketch, "E19.0.1.69", {"start": v(-11.68, 35.05) * mm, "end": v(-11.68, 25.9) * mm});
            skLineSegment(sketch, "E19.0.1.70", {"start": v(-19.81, 18.8) * mm, "end": v(-10.67, 18.8) * mm});
            skLineSegment(sketch, "E19.0.1.71", {"start": v(-19.81, 21.84) * mm, "end": v(-10.67, 21.84) * mm});
            skLineSegment(sketch, "E19.0.1.72", {"start": v(-23.88, 24.9) * mm, "end": v(-23.88, 15.75) * mm});
            skLineSegment(sketch, "E19.0.1.73", {"start": v(-29.97, 27.94) * mm, "end": v(-20.83, 27.94) * mm});
            skLineSegment(sketch, "E19.0.1.74", {"start": v(10.67, 33.02) * mm, "end": v(19.81, 33.02) * mm});
            skPoint(sketch, "E19.0.1.75", {"position": v(10.67, 32.51) * mm});
            skLineSegment(sketch, "E19.0.1.76", {"start": v(29.97, 35.05) * mm, "end": v(29.97, 25.9) * mm});
            skPoint(sketch, "E19.0.1.77", {"position": v(-19.81, 22.35) * mm});
            skLineSegment(sketch, "E19.0.1.78", {"start": v(20.83, 24.9) * mm, "end": v(29.97, 24.9) * mm});
            skLineSegment(sketch, "E19.0.1.79", {"start": v(0.5, 22.86) * mm, "end": v(9.65, 22.86) * mm});
            skLineSegment(sketch, "E19.0.1.80", {"start": v(-9.65, 35.05) * mm, "end": v(-0.5, 35.05) * mm});
            skLineSegment(sketch, "E19.0.1.81", {"start": v(-9.65, 26.92) * mm, "end": v(-0.5, 26.92) * mm});
            skLineSegment(sketch, "E19.0.1.82", {"start": v(6.6, 35.05) * mm, "end": v(6.6, 25.9) * mm});
            skLineSegment(sketch, "E19.0.1.83", {"start": v(0.5, 20.83) * mm, "end": v(9.65, 20.83) * mm});
            skLineSegment(sketch, "E19.0.1.84", {"start": v(20.83, 17.78) * mm, "end": v(29.97, 17.78) * mm});
            skLineSegment(sketch, "E19.0.1.85", {"start": v(5.59, 35.05) * mm, "end": v(5.59, 25.9) * mm});
            skLineSegment(sketch, "E19.0.1.86", {"start": v(8.64, 35.05) * mm, "end": v(8.64, 25.9) * mm});
            skLineSegment(sketch, "E19.0.1.87", {"start": v(-9.65, 33.02) * mm, "end": v(-0.5, 33.02) * mm});
            skPoint(sketch, "E19.0.1.88", {"position": v(29.97, 18.29) * mm});
            skLineSegment(sketch, "E19.0.1.89", {"start": v(14.73, 24.9) * mm, "end": v(14.73, 15.75) * mm});
            skLineSegment(sketch, "E19.0.1.90", {"start": v(-26.92, 24.9) * mm, "end": v(-26.92, 15.75) * mm});
            skLineSegment(sketch, "E19.0.1.91", {"start": v(-29.97, 35.05) * mm, "end": v(-20.83, 35.05) * mm});
            skPoint(sketch, "E19.0.1.92", {"position": v(-20.83, 28.45) * mm});
            skLineSegment(sketch, "E19.0.1.93", {"start": v(20.83, 35.05) * mm, "end": v(20.83, 25.9) * mm});
            skPoint(sketch, "E19.0.1.94", {"position": v(0.5, 30.48) * mm});
            skLineSegment(sketch, "E19.0.1.95", {"start": v(20.83, 15.75) * mm, "end": v(29.97, 15.75) * mm});
            skLineSegment(sketch, "E19.0.1.96", {"start": v(16.76, 24.9) * mm, "end": v(16.76, 15.75) * mm});
            skLineSegment(sketch, "E19.0.1.97", {"start": v(-19.81, 20.83) * mm, "end": v(-10.67, 20.83) * mm});
            skLineSegment(sketch, "E19.0.1.98", {"start": v(-21.84, 24.9) * mm, "end": v(-21.84, 15.75) * mm});
            skLineSegment(sketch, "E19.0.1.99", {"start": v(-19.81, 24.9) * mm, "end": v(-10.67, 24.9) * mm});
            skLineSegment(sketch, "E19.0.1.100", {"start": v(0.5, 19.81) * mm, "end": v(9.65, 19.81) * mm});
            skLineSegment(sketch, "E19.0.1.101", {"start": v(10.67, 26.92) * mm, "end": v(19.81, 26.92) * mm});
            skLineSegment(sketch, "E19.0.1.102", {"start": v(-9.65, 32) * mm, "end": v(-0.5, 32) * mm});
            skLineSegment(sketch, "E19.0.1.103", {"start": v(-9.65, 15.75) * mm, "end": v(-29.97, 15.75) * mm, "construction": true});
            skPoint(sketch, "E19.0.1.104", {"position": v(29.97, 22.35) * mm});
            skLineSegment(sketch, "E19.0.1.105", {"start": v(13.72, 24.9) * mm, "end": v(13.72, 15.75) * mm});
            skLineSegment(sketch, "E19.0.1.106", {"start": v(-27.94, 24.9) * mm, "end": v(-27.94, 15.75) * mm});
            skLineSegment(sketch, "E19.0.1.107", {"start": v(-29.97, 26.92) * mm, "end": v(-20.83, 26.92) * mm});
            skLineSegment(sketch, "E19.0.1.108", {"start": v(-29.97, 32) * mm, "end": v(-20.83, 32) * mm});
            skLineSegment(sketch, "E19.0.1.109", {"start": v(-20.83, 24.9) * mm, "end": v(-20.83, 15.75) * mm});
            skLineSegment(sketch, "E19.0.1.110", {"start": v(0.5, 17.78) * mm, "end": v(9.65, 17.78) * mm});
            skLineSegment(sketch, "E19.0.1.111", {"start": v(-0.5, 24.9) * mm, "end": v(-0.5, 15.75) * mm});
            skLineSegment(sketch, "E19.0.1.112", {"start": v(24.9, 35.05) * mm, "end": v(24.9, 25.9) * mm});
            skLineSegment(sketch, "E19.0.1.113", {"start": v(20.83, 18.8) * mm, "end": v(29.97, 18.8) * mm});
            skLineSegment(sketch, "E19.0.1.114", {"start": v(-9.65, 29.97) * mm, "end": v(-0.5, 29.97) * mm});
            skLineSegment(sketch, "E19.0.1.115", {"start": v(10.67, 24.9) * mm, "end": v(10.67, 15.75) * mm});
            skPoint(sketch, "E19.0.1.116", {"position": v(-9.65, 20.32) * mm});
            skLineSegment(sketch, "E19.0.1.117", {"start": v(26.92, 35.05) * mm, "end": v(26.92, 25.9) * mm});
            skLineSegment(sketch, "E19.0.1.118", {"start": v(9.65, 35.05) * mm, "end": v(9.65, 25.9) * mm});
            skLineSegment(sketch, "E19.0.1.119", {"start": v(0.5, 35.05) * mm, "end": v(0.5, 25.9) * mm});
            skLineSegment(sketch, "E19.0.1.120", {"start": v(28.96, 35.05) * mm, "end": v(28.96, 25.9) * mm});
            skPoint(sketch, "E19.0.1.121", {"position": v(20.83, 22.35) * mm});
            skLineSegment(sketch, "E19.0.1.122", {"start": v(-28.96, 24.9) * mm, "end": v(-28.96, 15.75) * mm});
            skPoint(sketch, "E19.0.1.123", {"position": v(-20.83, 32.51) * mm});
            skLineSegment(sketch, "E19.0.1.124", {"start": v(20.83, 23.88) * mm, "end": v(29.97, 23.88) * mm});
            skPoint(sketch, "E19.0.1.125", {"position": v(10.67, 20.32) * mm});
            skLineSegment(sketch, "E19.0.1.126", {"start": v(-13.72, 35.05) * mm, "end": v(-13.72, 25.9) * mm});
            skLineSegment(sketch, "E19.0.1.127", {"start": v(10.67, 30.99) * mm, "end": v(19.81, 30.99) * mm});
            skLineSegment(sketch, "E19.0.1.128", {"start": v(23.88, 35.05) * mm, "end": v(23.88, 25.9) * mm});
            skLineSegment(sketch, "E19.0.1.129", {"start": v(10.67, 34.04) * mm, "end": v(19.81, 34.04) * mm});
            skLineSegment(sketch, "E19.0.1.130", {"start": v(1.52, 35.05) * mm, "end": v(1.52, 25.9) * mm});
            skLineSegment(sketch, "E19.0.1.131", {"start": v(-12.7, 35.05) * mm, "end": v(-12.7, 25.9) * mm});
            skLineSegment(sketch, "E19.0.1.132", {"start": v(-18.8, 35.05) * mm, "end": v(-18.8, 25.9) * mm});
            skPoint(sketch, "E19.0.1.133", {"position": v(-29.97, 20.32) * mm});
            skLineSegment(sketch, "E19.0.1.134", {"start": v(12.7, 24.9) * mm, "end": v(12.7, 15.75) * mm});
            skLineSegment(sketch, "E19.0.1.135", {"start": v(-29.97, 24.9) * mm, "end": v(-29.97, 15.75) * mm});
            skLineSegment(sketch, "E19.0.1.136", {"start": v(-16.76, 35.05) * mm, "end": v(-16.76, 25.9) * mm});
            skLineSegment(sketch, "E19.0.1.137", {"start": v(-19.81, 16.76) * mm, "end": v(-10.67, 16.76) * mm});
            skPoint(sketch, "E19.0.1.138", {"position": v(9.65, 18.29) * mm});
            skPoint(sketch, "E19.0.1.139", {"position": v(-9.65, 32.51) * mm});
            skPoint(sketch, "E19.0.1.140", {"position": v(0.5, 22.35) * mm});
            skPoint(sketch, "E19.0.1.141", {"position": v(-10.67, 22.35) * mm});
            skPoint(sketch, "E19.0.1.142", {"position": v(-0.5, 32.51) * mm});
            skLineSegment(sketch, "E19.0.1.143", {"start": v(-19.81, 15.75) * mm, "end": v(-10.67, 15.75) * mm});
            skLineSegment(sketch, "E19.0.1.144", {"start": v(0.5, 15.75) * mm, "end": v(9.65, 15.75) * mm});
            skPoint(sketch, "E19.0.1.145", {"position": v(-0.5, 28.45) * mm});
            skPoint(sketch, "E19.0.1.146", {"position": v(9.65, 22.35) * mm});
            skPoint(sketch, "E19.0.1.147", {"position": v(-9.65, 20.32) * mm});
            skLineSegment(sketch, "E19.0.1.148", {"start": v(0.5, 18.8) * mm, "end": v(0.5, 17.78) * mm});
            skLineSegment(sketch, "E19.0.1.149", {"start": v(-1.52, 15.75) * mm, "end": v(-0.5, 15.75) * mm});
            skLineSegment(sketch, "E19.0.1.150", {"start": v(-9.65, 30.99) * mm, "end": v(-9.65, 29.97) * mm});
            skLineSegment(sketch, "E19.0.1.151", {"start": v(29.97, 22.86) * mm, "end": v(29.97, 21.84) * mm});
            skLineSegment(sketch, "E19.0.1.152", {"start": v(19.81, 35.05) * mm, "end": v(19.81, 34.04) * mm});
            skLineSegment(sketch, "E19.0.1.153", {"start": v(10.67, 28.96) * mm, "end": v(10.67, 27.94) * mm});
            skLineSegment(sketch, "E19.0.1.154", {"start": v(-19.81, 25.9) * mm, "end": v(-18.8, 25.9) * mm});
            skLineSegment(sketch, "E19.0.1.155", {"start": v(-19.81, 18.8) * mm, "end": v(-19.81, 17.78) * mm});
            skLineSegment(sketch, "E19.0.1.156", {"start": v(9.65, 20.83) * mm, "end": v(9.65, 19.81) * mm});
            skLineSegment(sketch, "E19.0.1.157", {"start": v(19.81, 26.92) * mm, "end": v(19.81, 25.9) * mm});
            skLineSegment(sketch, "E19.0.1.158", {"start": v(10.67, 15.75) * mm, "end": v(11.68, 15.75) * mm});
            skLineSegment(sketch, "E19.0.1.159", {"start": v(22.86, 35.05) * mm, "end": v(23.88, 35.05) * mm});
            skLineSegment(sketch, "E19.0.1.160", {"start": v(-29.97, 24.9) * mm, "end": v(-28.96, 24.9) * mm});
            skLineSegment(sketch, "E19.0.1.161", {"start": v(-29.97, 30.99) * mm, "end": v(-29.97, 29.97) * mm});
            skLineSegment(sketch, "E19.0.1.162", {"start": v(-5.59, 15.75) * mm, "end": v(-4.57, 15.75) * mm});
            skLineSegment(sketch, "E19.0.1.163", {"start": v(-5.59, 24.9) * mm, "end": v(-4.57, 24.9) * mm});
            skLineSegment(sketch, "E19.0.1.164", {"start": v(-7.62, 15.75) * mm, "end": v(-6.6, 15.75) * mm});
            skLineSegment(sketch, "E19.0.1.165", {"start": v(-20.83, 28.96) * mm, "end": v(-20.83, 27.94) * mm});
            skLineSegment(sketch, "E19.0.1.166", {"start": v(-7.62, 24.9) * mm, "end": v(-6.6, 24.9) * mm});
            skLineSegment(sketch, "E19.0.1.167", {"start": v(-9.65, 15.75) * mm, "end": v(-7.62, 15.75) * mm, "construction": true});
            skLineSegment(sketch, "E19.0.1.168", {"start": v(-1.52, 24.9) * mm, "end": v(-0.5, 24.9) * mm});
            skLineSegment(sketch, "E19.0.1.169", {"start": v(2.54, 25.9) * mm, "end": v(3.56, 25.9) * mm});
            skLineSegment(sketch, "E19.0.1.170", {"start": v(-9.65, 15.75) * mm, "end": v(-8.64, 15.75) * mm});
            skLineSegment(sketch, "E19.0.1.171", {"start": v(-9.65, 24.9) * mm, "end": v(-8.64, 24.9) * mm});
            skLineSegment(sketch, "E19.0.1.172", {"start": v(-3.56, 15.75) * mm, "end": v(-2.54, 15.75) * mm});
            skLineSegment(sketch, "E19.0.1.173", {"start": v(10.67, 26.92) * mm, "end": v(10.67, 25.9) * mm});
            skLineSegment(sketch, "E19.0.1.174", {"start": v(14.73, 15.75) * mm, "end": v(15.75, 15.75) * mm});
            skLineSegment(sketch, "E19.0.1.175", {"start": v(0.5, 25.9) * mm, "end": v(2.54, 25.9) * mm, "construction": true});
            skLineSegment(sketch, "E19.0.1.176", {"start": v(-11.68, 35.05) * mm, "end": v(-10.67, 35.05) * mm});
            skLineSegment(sketch, "E19.0.1.177", {"start": v(-17.78, 35.05) * mm, "end": v(-16.76, 35.05) * mm});
            skLineSegment(sketch, "E19.0.1.178", {"start": v(-25.9, 24.9) * mm, "end": v(-24.9, 24.9) * mm});
            skLineSegment(sketch, "E19.0.1.179", {"start": v(-29.97, 33.02) * mm, "end": v(-29.97, 32) * mm});
            skLineSegment(sketch, "E19.0.1.180", {"start": v(-19.81, 35.05) * mm, "end": v(-18.8, 35.05) * mm});
            skLineSegment(sketch, "E19.0.1.181", {"start": v(29.97, 18.8) * mm, "end": v(29.97, 17.78) * mm});
            skLineSegment(sketch, "E19.0.1.182", {"start": v(10.67, 15.75) * mm, "end": v(12.7, 15.75) * mm, "construction": true});
            skLineSegment(sketch, "E19.0.1.183", {"start": v(29.97, 16.76) * mm, "end": v(29.97, 15.75) * mm});
            skLineSegment(sketch, "E19.0.1.184", {"start": v(-0.5, 35.05) * mm, "end": v(-0.5, 34.04) * mm});
            skLineSegment(sketch, "E19.0.1.185", {"start": v(-0.5, 26.92) * mm, "end": v(-0.5, 25.9) * mm});
            skLineSegment(sketch, "E19.0.1.186", {"start": v(6.6, 25.9) * mm, "end": v(7.62, 25.9) * mm});
            skLineSegment(sketch, "E19.0.1.187", {"start": v(19.81, 28.96) * mm, "end": v(19.81, 27.94) * mm});
            skLineSegment(sketch, "E19.0.1.188", {"start": v(10.67, 35.05) * mm, "end": v(10.67, 34.04) * mm});
            skLineSegment(sketch, "E19.0.1.189", {"start": v(-19.81, 24.9) * mm, "end": v(-19.81, 23.88) * mm});
            skLineSegment(sketch, "E19.0.1.190", {"start": v(-10.67, 24.9) * mm, "end": v(-10.67, 23.88) * mm});
            skLineSegment(sketch, "E19.0.1.191", {"start": v(-25.9, 15.75) * mm, "end": v(-24.9, 15.75) * mm});
            skLineSegment(sketch, "E19.0.1.192", {"start": v(-13.72, 25.9) * mm, "end": v(-12.7, 25.9) * mm});
            skLineSegment(sketch, "E19.0.1.193", {"start": v(19.81, 30.99) * mm, "end": v(19.81, 29.97) * mm});
            skLineSegment(sketch, "E19.0.1.194", {"start": v(-23.88, 24.9) * mm, "end": v(-22.86, 24.9) * mm});
            skLineSegment(sketch, "E19.0.1.195", {"start": v(18.8, 24.9) * mm, "end": v(19.81, 24.9) * mm});
            skLineSegment(sketch, "E19.0.1.196", {"start": v(24.9, 35.05) * mm, "end": v(25.9, 35.05) * mm});
            skLineSegment(sketch, "E19.0.1.197", {"start": v(-9.65, 35.05) * mm, "end": v(-9.65, 34.04) * mm});
            skLineSegment(sketch, "E19.0.1.198", {"start": v(-9.65, 26.92) * mm, "end": v(-9.65, 25.9) * mm});
            skLineSegment(sketch, "E19.0.1.199", {"start": v(-11.68, 25.9) * mm, "end": v(-10.67, 25.9) * mm});
            skLineSegment(sketch, "E19.0.1.200", {"start": v(-20.83, 26.92) * mm, "end": v(-20.83, 25.9) * mm});
            skLineSegment(sketch, "E19.0.1.201", {"start": v(20.83, 22.86) * mm, "end": v(20.83, 21.84) * mm});
            skLineSegment(sketch, "E19.0.1.202", {"start": v(10.67, 30.99) * mm, "end": v(10.67, 29.97) * mm});
            skLineSegment(sketch, "E19.0.1.203", {"start": v(20.83, 20.83) * mm, "end": v(20.83, 19.81) * mm});
            skLineSegment(sketch, "E19.0.1.204", {"start": v(6.6, 35.05) * mm, "end": v(7.62, 35.05) * mm});
            skLineSegment(sketch, "E19.0.1.205", {"start": v(4.57, 35.05) * mm, "end": v(5.59, 35.05) * mm});
            skLineSegment(sketch, "E19.0.1.206", {"start": v(-10.67, 20.83) * mm, "end": v(-10.67, 19.81) * mm});
            skLineSegment(sketch, "E19.0.1.207", {"start": v(-20.83, 35.05) * mm, "end": v(-20.83, 34.04) * mm});
            skLineSegment(sketch, "E19.0.1.208", {"start": v(19.81, 33.02) * mm, "end": v(19.81, 32) * mm});
            skLineSegment(sketch, "E19.0.1.209", {"start": v(20.83, 18.8) * mm, "end": v(20.83, 17.78) * mm});
            skLineSegment(sketch, "E19.0.1.210", {"start": v(-19.81, 16.76) * mm, "end": v(-19.81, 15.75) * mm});
            skLineSegment(sketch, "E19.0.1.211", {"start": v(-10.67, 16.76) * mm, "end": v(-10.67, 15.75) * mm});
            skLineSegment(sketch, "E19.0.1.212", {"start": v(10.67, 33.02) * mm, "end": v(10.67, 32) * mm});
            skLineSegment(sketch, "E19.0.1.213", {"start": v(16.76, 15.75) * mm, "end": v(17.78, 15.75) * mm});
            skLineSegment(sketch, "E19.0.1.214", {"start": v(-19.81, 22.86) * mm, "end": v(-19.81, 21.84) * mm});
            skLineSegment(sketch, "E19.0.1.215", {"start": v(-23.88, 15.75) * mm, "end": v(-22.86, 15.75) * mm});
            skLineSegment(sketch, "E19.0.1.216", {"start": v(-21.84, 24.9) * mm, "end": v(-20.83, 24.9) * mm});
            skLineSegment(sketch, "E19.0.1.217", {"start": v(-10.67, 22.86) * mm, "end": v(-10.67, 21.84) * mm});
            skLineSegment(sketch, "E19.0.1.218", {"start": v(-9.65, 28.96) * mm, "end": v(-9.65, 27.94) * mm});
            skLineSegment(sketch, "E19.0.1.219", {"start": v(0.5, 35.05) * mm, "end": v(1.52, 35.05) * mm});
            skLineSegment(sketch, "E19.0.1.220", {"start": v(0.5, 16.76) * mm, "end": v(0.5, 15.75) * mm});
            skLineSegment(sketch, "E19.0.1.221", {"start": v(0.5, 24.9) * mm, "end": v(0.5, 23.88) * mm});
            skLineSegment(sketch, "E19.0.1.222", {"start": v(16.76, 24.9) * mm, "end": v(17.78, 24.9) * mm});
            skLineSegment(sketch, "E19.0.1.223", {"start": v(12.7, 15.75) * mm, "end": v(13.72, 15.75) * mm});
            skLineSegment(sketch, "E19.0.1.224", {"start": v(18.8, 15.75) * mm, "end": v(19.81, 15.75) * mm});
            skLineSegment(sketch, "E19.0.1.225", {"start": v(-27.94, 15.75) * mm, "end": v(-26.92, 15.75) * mm});
            skLineSegment(sketch, "E19.0.1.226", {"start": v(-13.72, 35.05) * mm, "end": v(-12.7, 35.05) * mm});
            skLineSegment(sketch, "E19.0.1.227", {"start": v(-29.97, 35.05) * mm, "end": v(-29.97, 34.04) * mm});
            skLineSegment(sketch, "E19.0.1.228", {"start": v(28.96, 35.05) * mm, "end": v(29.97, 35.05) * mm});
            skLineSegment(sketch, "E19.0.1.229", {"start": v(8.64, 35.05) * mm, "end": v(9.65, 35.05) * mm});
            skLineSegment(sketch, "E19.0.1.230", {"start": v(0.5, 25.9) * mm, "end": v(1.52, 25.9) * mm});
            skLineSegment(sketch, "E19.0.1.231", {"start": v(29.97, 24.9) * mm, "end": v(29.97, 23.88) * mm});
            skLineSegment(sketch, "E19.0.1.232", {"start": v(24.9, 25.9) * mm, "end": v(25.9, 25.9) * mm});
            skLineSegment(sketch, "E19.0.1.233", {"start": v(12.7, 24.9) * mm, "end": v(13.72, 24.9) * mm});
            skLineSegment(sketch, "E19.0.1.234", {"start": v(28.96, 25.9) * mm, "end": v(29.97, 25.9) * mm});
            skLineSegment(sketch, "E19.0.1.235", {"start": v(-29.97, 28.96) * mm, "end": v(-29.97, 27.94) * mm});
            skLineSegment(sketch, "E19.0.1.236", {"start": v(-19.81, 25.9) * mm, "end": v(-17.78, 25.9) * mm, "construction": true});
            skLineSegment(sketch, "E19.0.1.237", {"start": v(-19.81, 20.83) * mm, "end": v(-19.81, 19.81) * mm});
            skLineSegment(sketch, "E19.0.1.238", {"start": v(-17.78, 25.9) * mm, "end": v(-16.76, 25.9) * mm});
            skLineSegment(sketch, "E19.0.1.239", {"start": v(-29.97, 26.92) * mm, "end": v(-29.97, 25.9) * mm});
            skLineSegment(sketch, "E19.0.1.240", {"start": v(-21.84, 15.75) * mm, "end": v(-20.83, 15.75) * mm});
            skLineSegment(sketch, "E19.0.1.241", {"start": v(-15.75, 25.9) * mm, "end": v(-14.73, 25.9) * mm});
            skLineSegment(sketch, "E19.0.1.242", {"start": v(2.54, 35.05) * mm, "end": v(3.56, 35.05) * mm});
            skLineSegment(sketch, "E19.0.1.243", {"start": v(26.92, 25.9) * mm, "end": v(27.94, 25.9) * mm});
            skLineSegment(sketch, "E19.0.1.244", {"start": v(10.67, 24.9) * mm, "end": v(11.68, 24.9) * mm});
            skLineSegment(sketch, "E19.0.1.245", {"start": v(20.83, 16.76) * mm, "end": v(20.83, 15.75) * mm});
            skLineSegment(sketch, "E19.0.1.246", {"start": v(0.5, 20.83) * mm, "end": v(0.5, 19.81) * mm});
            skLineSegment(sketch, "E19.0.1.247", {"start": v(9.65, 16.76) * mm, "end": v(9.65, 15.75) * mm});
            skLineSegment(sketch, "E19.0.1.248", {"start": v(9.65, 24.9) * mm, "end": v(9.65, 23.88) * mm});
            skLineSegment(sketch, "E19.0.1.249", {"start": v(-9.65, 33.02) * mm, "end": v(-9.65, 32) * mm});
            skLineSegment(sketch, "E19.0.1.250", {"start": v(29.97, 20.83) * mm, "end": v(29.97, 19.81) * mm});
            skLineSegment(sketch, "E19.0.1.251", {"start": v(20.83, 35.05) * mm, "end": v(21.84, 35.05) * mm});
            skLineSegment(sketch, "E19.0.1.252", {"start": v(26.92, 35.05) * mm, "end": v(27.94, 35.05) * mm});
            skLineSegment(sketch, "E19.0.1.253", {"start": v(-27.94, 24.9) * mm, "end": v(-26.92, 24.9) * mm});
            skLineSegment(sketch, "E19.0.1.254", {"start": v(-29.97, 15.75) * mm, "end": v(-27.94, 15.75) * mm, "construction": true});
            skLineSegment(sketch, "E19.0.1.255", {"start": v(20.83, 25.9) * mm, "end": v(21.84, 25.9) * mm});
            skLineSegment(sketch, "E19.0.1.256", {"start": v(-15.75, 35.05) * mm, "end": v(-14.73, 35.05) * mm});
            skLineSegment(sketch, "E19.0.1.257", {"start": v(8.64, 25.9) * mm, "end": v(9.65, 25.9) * mm});
            skLineSegment(sketch, "E19.0.1.258", {"start": v(14.73, 24.9) * mm, "end": v(15.75, 24.9) * mm});
            skLineSegment(sketch, "E19.0.1.259", {"start": v(20.83, 24.9) * mm, "end": v(20.83, 23.88) * mm});
            skLineSegment(sketch, "E19.0.1.260", {"start": v(20.83, 25.9) * mm, "end": v(22.86, 25.9) * mm, "construction": true});
            skLineSegment(sketch, "E19.0.1.261", {"start": v(-29.97, 15.75) * mm, "end": v(-28.96, 15.75) * mm});
            skLineSegment(sketch, "E19.0.1.262", {"start": v(-10.67, 18.8) * mm, "end": v(-10.67, 17.78) * mm});
            skLineSegment(sketch, "E19.0.1.263", {"start": v(-20.83, 30.99) * mm, "end": v(-20.83, 29.97) * mm});
            skLineSegment(sketch, "E19.0.1.264", {"start": v(22.86, 25.9) * mm, "end": v(23.88, 25.9) * mm});
            skLineSegment(sketch, "E19.0.1.265", {"start": v(-20.83, 33.02) * mm, "end": v(-20.83, 32) * mm});
            skLineSegment(sketch, "E19.0.1.266", {"start": v(9.65, 18.8) * mm, "end": v(9.65, 17.78) * mm});
            skLineSegment(sketch, "E19.0.1.267", {"start": v(-0.5, 30.99) * mm, "end": v(-0.5, 29.97) * mm});
            skLineSegment(sketch, "E19.0.1.268", {"start": v(-3.56, 24.9) * mm, "end": v(-2.54, 24.9) * mm});
            skLineSegment(sketch, "E19.0.1.269", {"start": v(9.65, 22.86) * mm, "end": v(9.65, 21.84) * mm});
            skLineSegment(sketch, "E19.0.1.270", {"start": v(0.5, 22.86) * mm, "end": v(0.5, 21.84) * mm});
            skLineSegment(sketch, "E19.0.1.271", {"start": v(4.57, 25.9) * mm, "end": v(5.59, 25.9) * mm});
            skLineSegment(sketch, "E19.0.1.272", {"start": v(-0.5, 28.96) * mm, "end": v(-0.5, 27.94) * mm});
            skLineSegment(sketch, "E19.0.1.273", {"start": v(-0.5, 33.02) * mm, "end": v(-0.5, 32) * mm});
            skLineSegment(sketch, "E19.direction1", {"start": v(-29.97, -4.57) * mm, "end": v(-4.57, -4.57) * mm, "construction": true});
            skLineSegment(sketch, "E19.direction2", {"start": v(-29.97, -4.57) * mm, "end": v(-29.97, 15.75) * mm, "construction": true});
            skLineSegment(sketch, "E20.0.1.0", {"start": v(-19.81, -22.86) * mm, "end": v(-10.67, -22.86) * mm});
            skLineSegment(sketch, "E20.0.1.1", {"start": v(-14.73, -5.59) * mm, "end": v(-14.73, -14.73) * mm});
            skLineSegment(sketch, "E20.0.1.2", {"start": v(17.78, -15.75) * mm, "end": v(17.78, -24.9) * mm});
            skLineSegment(sketch, "E20.0.1.3", {"start": v(19.81, -15.75) * mm, "end": v(19.81, -24.9) * mm});
            skLineSegment(sketch, "E20.0.1.4", {"start": v(20.83, -20.83) * mm, "end": v(29.97, -20.83) * mm});
            skLineSegment(sketch, "E20.0.1.5", {"start": v(3.56, -5.59) * mm, "end": v(3.56, -14.73) * mm});
            skLineSegment(sketch, "E20.0.1.6", {"start": v(10.67, -5.59) * mm, "end": v(19.81, -5.59) * mm});
            skLineSegment(sketch, "E20.0.1.7", {"start": v(-20.83, -15.75) * mm, "end": v(-20.83, -24.9) * mm});
            skLineSegment(sketch, "E20.0.1.8", {"start": v(10.67, -11.68) * mm, "end": v(19.81, -11.68) * mm});
            skLineSegment(sketch, "E20.0.1.9", {"start": v(-29.97, -8.64) * mm, "end": v(-20.83, -8.64) * mm});
            skPoint(sketch, "E20.0.1.10", {"position": v(29.97, -18.29) * mm});
            skPoint(sketch, "E20.0.1.11", {"position": v(10.67, -8.13) * mm});
            skLineSegment(sketch, "E20.0.1.12", {"start": v(2.54, -5.59) * mm, "end": v(2.54, -14.73) * mm});
            skLineSegment(sketch, "E20.0.1.13", {"start": v(-9.65, -9.65) * mm, "end": v(-0.5, -9.65) * mm});
            skPoint(sketch, "E20.0.1.14", {"position": v(-19.81, -18.29) * mm});
            skLineSegment(sketch, "E20.0.1.15", {"start": v(20.83, -18.8) * mm, "end": v(29.97, -18.8) * mm});
            skLineSegment(sketch, "E20.0.1.16", {"start": v(0.5, -21.84) * mm, "end": v(9.65, -21.84) * mm});
            skLineSegment(sketch, "E20.0.1.17", {"start": v(0.5, -19.81) * mm, "end": v(9.65, -19.81) * mm});
            skLineSegment(sketch, "E20.0.1.18", {"start": v(4.57, -5.59) * mm, "end": v(4.57, -14.73) * mm});
            skLineSegment(sketch, "E20.0.1.19", {"start": v(20.83, -22.86) * mm, "end": v(29.97, -22.86) * mm});
            skLineSegment(sketch, "E20.0.1.20", {"start": v(8.64, -5.59) * mm, "end": v(8.64, -14.73) * mm});
            skLineSegment(sketch, "E20.0.1.21", {"start": v(-9.65, -7.62) * mm, "end": v(-0.5, -7.62) * mm});
            skLineSegment(sketch, "E20.0.1.22", {"start": v(14.73, -15.75) * mm, "end": v(14.73, -24.9) * mm});
            skLineSegment(sketch, "E20.0.1.23", {"start": v(-29.97, -24.9) * mm, "end": v(-29.97, -4.57) * mm, "construction": true});
            skLineSegment(sketch, "E20.0.1.24", {"start": v(-26.92, -15.75) * mm, "end": v(-26.92, -24.9) * mm});
            skLineSegment(sketch, "E20.0.1.25", {"start": v(-29.97, -5.59) * mm, "end": v(-20.83, -5.59) * mm});
            skPoint(sketch, "E20.0.1.26", {"position": v(20.83, -10.16) * mm});
            skLineSegment(sketch, "E20.0.1.27", {"start": v(-29.97, -10.67) * mm, "end": v(-20.83, -10.67) * mm});
            skLineSegment(sketch, "E20.0.1.28", {"start": v(-22.86, -15.75) * mm, "end": v(-22.86, -24.9) * mm});
            skLineSegment(sketch, "E20.0.1.29", {"start": v(11.68, -15.75) * mm, "end": v(11.68, -24.9) * mm});
            skLineSegment(sketch, "E20.0.1.30", {"start": v(0.5, -20.83) * mm, "end": v(9.65, -20.83) * mm});
            skLineSegment(sketch, "E20.0.1.31", {"start": v(10.67, -13.72) * mm, "end": v(19.81, -13.72) * mm});
            skLineSegment(sketch, "E20.0.1.32", {"start": v(-9.65, -8.64) * mm, "end": v(-0.5, -8.64) * mm});
            skLineSegment(sketch, "E20.0.1.33", {"start": v(13.72, -15.75) * mm, "end": v(13.72, -24.9) * mm});
            skLineSegment(sketch, "E20.0.1.34", {"start": v(-27.94, -15.75) * mm, "end": v(-27.94, -24.9) * mm});
            skLineSegment(sketch, "E20.0.1.35", {"start": v(-29.97, -13.72) * mm, "end": v(-20.83, -13.72) * mm});
            skPoint(sketch, "E20.0.1.36", {"position": v(29.97, -22.35) * mm});
            skLineSegment(sketch, "E20.0.1.37", {"start": v(-1.52, -15.75) * mm, "end": v(-1.52, -24.9) * mm});
            skPoint(sketch, "E20.0.1.38", {"position": v(19.81, -8.13) * mm});
            skLineSegment(sketch, "E20.0.1.39", {"start": v(26.92, -5.59) * mm, "end": v(26.92, -14.73) * mm});
            skLineSegment(sketch, "E20.0.1.40", {"start": v(9.65, -5.59) * mm, "end": v(9.65, -14.73) * mm});
            skLineSegment(sketch, "E20.0.1.41", {"start": v(0.5, -5.59) * mm, "end": v(0.5, -14.73) * mm});
            skLineSegment(sketch, "E20.0.1.42", {"start": v(28.96, -5.59) * mm, "end": v(28.96, -14.73) * mm});
            skLineSegment(sketch, "E20.0.1.43", {"start": v(-16.76, -5.59) * mm, "end": v(-16.76, -14.73) * mm});
            skLineSegment(sketch, "E20.0.1.44", {"start": v(12.7, -15.75) * mm, "end": v(12.7, -24.9) * mm});
            skLineSegment(sketch, "E20.0.1.45", {"start": v(-29.97, -9.65) * mm, "end": v(-20.83, -9.65) * mm});
            skLineSegment(sketch, "E20.0.1.46", {"start": v(-19.81, -20.83) * mm, "end": v(-10.67, -20.83) * mm});
            skLineSegment(sketch, "E20.0.1.47", {"start": v(20.83, -23.88) * mm, "end": v(29.97, -23.88) * mm});
            skLineSegment(sketch, "E20.0.1.48", {"start": v(1.52, -5.59) * mm, "end": v(1.52, -14.73) * mm});
            skLineSegment(sketch, "E20.0.1.49", {"start": v(-9.65, -24.9) * mm, "end": v(10.67, -24.9) * mm, "construction": true});
            skLineSegment(sketch, "E20.0.1.50", {"start": v(10.67, -10.67) * mm, "end": v(19.81, -10.67) * mm});
            skLineSegment(sketch, "E20.0.1.51", {"start": v(10.67, -8.64) * mm, "end": v(19.81, -8.64) * mm});
            skLineSegment(sketch, "E20.0.1.52", {"start": v(10.67, -6.6) * mm, "end": v(19.81, -6.6) * mm});
            skPoint(sketch, "E20.0.1.53", {"position": v(20.83, -18.29) * mm});
            skLineSegment(sketch, "E20.0.1.54", {"start": v(10.67, -15.75) * mm, "end": v(10.67, -24.9) * mm});
            skLineSegment(sketch, "E20.0.1.55", {"start": v(-9.65, -10.67) * mm, "end": v(-0.5, -10.67) * mm});
            skPoint(sketch, "E20.0.1.56", {"position": v(19.81, -12.2) * mm});
            skLineSegment(sketch, "E20.0.1.57", {"start": v(20.83, -21.84) * mm, "end": v(29.97, -21.84) * mm});
            skLineSegment(sketch, "E20.0.1.58", {"start": v(24.9, -5.59) * mm, "end": v(24.9, -14.73) * mm});
            skLineSegment(sketch, "E20.0.1.59", {"start": v(-0.5, -15.75) * mm, "end": v(-0.5, -24.9) * mm});
            skLineSegment(sketch, "E20.0.1.60", {"start": v(0.5, -22.86) * mm, "end": v(9.65, -22.86) * mm});
            skPoint(sketch, "E20.0.1.61", {"position": v(-29.97, -20.32) * mm});
            skLineSegment(sketch, "E20.0.1.62", {"start": v(-13.72, -5.59) * mm, "end": v(-13.72, -14.73) * mm});
            skLineSegment(sketch, "E20.0.1.63", {"start": v(-28.96, -15.75) * mm, "end": v(-28.96, -24.9) * mm});
            skLineSegment(sketch, "E20.0.1.64", {"start": v(0.5, -15.75) * mm, "end": v(9.65, -15.75) * mm});
            skLineSegment(sketch, "E20.0.1.65", {"start": v(0.5, -23.88) * mm, "end": v(9.65, -23.88) * mm});
            skLineSegment(sketch, "E20.0.1.66", {"start": v(-9.65, -11.68) * mm, "end": v(-0.5, -11.68) * mm});
            skLineSegment(sketch, "E20.0.1.67", {"start": v(-29.97, -11.68) * mm, "end": v(-20.83, -11.68) * mm});
            skLineSegment(sketch, "E20.0.1.68", {"start": v(27.94, -5.59) * mm, "end": v(27.94, -14.73) * mm});
            skLineSegment(sketch, "E20.0.1.69", {"start": v(-29.97, -7.62) * mm, "end": v(-20.83, -7.62) * mm});
            skLineSegment(sketch, "E20.0.1.70", {"start": v(-17.78, -5.59) * mm, "end": v(-17.78, -14.73) * mm});
            skPoint(sketch, "E20.0.1.71", {"position": v(-9.65, -20.32) * mm});
            skLineSegment(sketch, "E20.0.1.72", {"start": v(0.5, -16.76) * mm, "end": v(9.65, -16.76) * mm});
            skLineSegment(sketch, "E20.0.1.73", {"start": v(20.83, -19.81) * mm, "end": v(29.97, -19.81) * mm});
            skLineSegment(sketch, "E20.0.1.74", {"start": v(10.67, -14.73) * mm, "end": v(19.81, -14.73) * mm});
            skLineSegment(sketch, "E20.0.1.75", {"start": v(-9.65, -12.7) * mm, "end": v(-0.5, -12.7) * mm});
            skLineSegment(sketch, "E20.0.1.76", {"start": v(-15.75, -5.59) * mm, "end": v(-15.75, -14.73) * mm});
            skLineSegment(sketch, "E20.0.1.77", {"start": v(20.83, -17.78) * mm, "end": v(29.97, -17.78) * mm});
            skLineSegment(sketch, "E20.0.1.78", {"start": v(-11.68, -5.59) * mm, "end": v(-11.68, -14.73) * mm});
            skLineSegment(sketch, "E20.0.1.79", {"start": v(-19.81, -21.84) * mm, "end": v(-10.67, -21.84) * mm});
            skLineSegment(sketch, "E20.0.1.80", {"start": v(5.59, -5.59) * mm, "end": v(5.59, -14.73) * mm});
            skPoint(sketch, "E20.0.1.81", {"position": v(-19.81, -10.16) * mm});
            skLineSegment(sketch, "E20.0.1.82", {"start": v(20.83, -5.59) * mm, "end": v(20.83, -14.73) * mm});
            skLineSegment(sketch, "E20.0.1.83", {"start": v(20.83, -24.9) * mm, "end": v(29.97, -24.9) * mm});
            skLineSegment(sketch, "E20.0.1.84", {"start": v(16.76, -15.75) * mm, "end": v(16.76, -24.9) * mm});
            skLineSegment(sketch, "E20.0.1.85", {"start": v(-19.81, -19.81) * mm, "end": v(-10.67, -19.81) * mm});
            skLineSegment(sketch, "E20.0.1.86", {"start": v(-21.84, -15.75) * mm, "end": v(-21.84, -24.9) * mm});
            skLineSegment(sketch, "E20.0.1.87", {"start": v(-19.81, -15.75) * mm, "end": v(-10.67, -15.75) * mm});
            skLineSegment(sketch, "E20.0.1.88", {"start": v(-9.65, -24.9) * mm, "end": v(-29.97, -24.9) * mm, "construction": true});
            skLineSegment(sketch, "E20.0.1.89", {"start": v(20.83, -16.76) * mm, "end": v(29.97, -16.76) * mm});
            skLineSegment(sketch, "E20.0.1.90", {"start": v(10.67, -9.65) * mm, "end": v(19.81, -9.65) * mm});
            skLineSegment(sketch, "E20.0.1.91", {"start": v(23.88, -5.59) * mm, "end": v(23.88, -14.73) * mm});
            skPoint(sketch, "E20.0.1.92", {"position": v(-9.65, -8.13) * mm});
            skPoint(sketch, "E20.0.1.93", {"position": v(-10.67, -18.29) * mm});
            skLineSegment(sketch, "E20.0.1.94", {"start": v(-12.7, -5.59) * mm, "end": v(-12.7, -14.73) * mm});
            skLineSegment(sketch, "E20.0.1.95", {"start": v(-18.8, -5.59) * mm, "end": v(-18.8, -14.73) * mm});
            skLineSegment(sketch, "E20.0.1.96", {"start": v(-19.81, -23.88) * mm, "end": v(-10.67, -23.88) * mm});
            skLineSegment(sketch, "E20.0.1.97", {"start": v(6.6, -5.59) * mm, "end": v(6.6, -14.73) * mm});
            skLineSegment(sketch, "E20.0.1.98", {"start": v(-9.65, -13.72) * mm, "end": v(-0.5, -13.72) * mm});
            skLineSegment(sketch, "E20.0.1.99", {"start": v(-9.65, -5.59) * mm, "end": v(-0.5, -5.59) * mm});
            skLineSegment(sketch, "E20.0.1.100", {"start": v(0.5, -17.78) * mm, "end": v(9.65, -17.78) * mm});
            skLineSegment(sketch, "E20.0.1.101", {"start": v(20.83, -15.75) * mm, "end": v(29.97, -15.75) * mm});
            skLineSegment(sketch, "E20.0.1.102", {"start": v(29.97, -5.59) * mm, "end": v(29.97, -14.73) * mm});
            skLineSegment(sketch, "E20.0.1.103", {"start": v(10.67, -7.62) * mm, "end": v(19.81, -7.62) * mm});
            skLineSegment(sketch, "E20.0.1.104", {"start": v(-29.97, -12.7) * mm, "end": v(-20.83, -12.7) * mm});
            skLineSegment(sketch, "E20.0.1.105", {"start": v(-23.88, -15.75) * mm, "end": v(-23.88, -24.9) * mm});
            skLineSegment(sketch, "E20.0.1.106", {"start": v(-19.81, -18.8) * mm, "end": v(-10.67, -18.8) * mm});
            skPoint(sketch, "E20.0.1.107", {"position": v(-29.97, -8.13) * mm});
            skPoint(sketch, "E20.0.1.108", {"position": v(-10.67, -22.35) * mm});
            skLineSegment(sketch, "E20.0.1.109", {"start": v(-9.65, -14.73) * mm, "end": v(-0.5, -14.73) * mm});
            skLineSegment(sketch, "E20.0.1.110", {"start": v(-9.65, -6.6) * mm, "end": v(-0.5, -6.6) * mm});
            skLineSegment(sketch, "E20.0.1.111", {"start": v(0.5, -18.8) * mm, "end": v(9.65, -18.8) * mm});
            skLineSegment(sketch, "E20.0.1.112", {"start": v(10.67, -12.7) * mm, "end": v(19.81, -12.7) * mm});
            skLineSegment(sketch, "E20.0.1.113", {"start": v(25.9, -5.59) * mm, "end": v(25.9, -14.73) * mm});
            skLineSegment(sketch, "E20.0.1.114", {"start": v(-19.81, -16.76) * mm, "end": v(-10.67, -16.76) * mm});
            skLineSegment(sketch, "E20.0.1.115", {"start": v(-24.9, -15.75) * mm, "end": v(-24.9, -24.9) * mm});
            skLineSegment(sketch, "E20.0.1.116", {"start": v(-29.97, -6.6) * mm, "end": v(-20.83, -6.6) * mm});
            skPoint(sketch, "E20.0.1.117", {"position": v(0.5, -10.16) * mm});
            skPoint(sketch, "E20.0.1.118", {"position": v(-20.83, -12.2) * mm});
            skLineSegment(sketch, "E20.0.1.119", {"start": v(7.62, -5.59) * mm, "end": v(7.62, -14.73) * mm});
            skLineSegment(sketch, "E20.0.1.120", {"start": v(18.8, -15.75) * mm, "end": v(18.8, -24.9) * mm});
            skLineSegment(sketch, "E20.0.1.121", {"start": v(21.84, -5.59) * mm, "end": v(21.84, -14.73) * mm});
            skLineSegment(sketch, "E20.0.1.122", {"start": v(-25.9, -15.75) * mm, "end": v(-25.9, -24.9) * mm});
            skLineSegment(sketch, "E20.0.1.123", {"start": v(-29.97, -14.73) * mm, "end": v(-20.83, -14.73) * mm});
            skPoint(sketch, "E20.0.1.124", {"position": v(10.67, -20.32) * mm});
            skPoint(sketch, "E20.0.1.125", {"position": v(-20.83, -8.13) * mm});
            skLineSegment(sketch, "E20.0.1.126", {"start": v(15.75, -15.75) * mm, "end": v(15.75, -24.9) * mm});
            skLineSegment(sketch, "E20.0.1.127", {"start": v(22.86, -5.59) * mm, "end": v(22.86, -14.73) * mm});
            skLineSegment(sketch, "E20.0.1.128", {"start": v(-19.81, -5.59) * mm, "end": v(-19.81, -14.73) * mm});
            skLineSegment(sketch, "E20.0.1.129", {"start": v(-10.67, -5.59) * mm, "end": v(-10.67, -14.73) * mm});
            skLineSegment(sketch, "E20.0.1.130", {"start": v(-19.81, -17.78) * mm, "end": v(-10.67, -17.78) * mm});
            skLineSegment(sketch, "E20.0.1.131", {"start": v(-2.54, -15.75) * mm, "end": v(-2.54, -24.9) * mm});
            skLineSegment(sketch, "E20.0.1.132", {"start": v(-9.65, -15.75) * mm, "end": v(-9.65, -24.9) * mm});
            skLineSegment(sketch, "E20.0.1.133", {"start": v(-8.64, -15.75) * mm, "end": v(-8.64, -24.9) * mm});
            skLineSegment(sketch, "E20.0.1.134", {"start": v(-7.62, -15.75) * mm, "end": v(-7.62, -24.9) * mm});
            skLineSegment(sketch, "E20.0.1.135", {"start": v(-6.6, -15.75) * mm, "end": v(-6.6, -24.9) * mm});
            skLineSegment(sketch, "E20.0.1.136", {"start": v(-5.59, -15.75) * mm, "end": v(-5.59, -24.9) * mm});
            skLineSegment(sketch, "E20.0.1.137", {"start": v(-4.57, -15.75) * mm, "end": v(-4.57, -24.9) * mm});
            skLineSegment(sketch, "E20.0.1.138", {"start": v(-3.56, -15.75) * mm, "end": v(-3.56, -24.9) * mm});
            skLineSegment(sketch, "E20.0.1.139", {"start": v(-29.97, -24.9) * mm, "end": v(-4.57, -24.9) * mm, "construction": true});
            skPoint(sketch, "E20.0.1.140", {"position": v(-9.65, -8.13) * mm});
            skPoint(sketch, "E20.0.1.141", {"position": v(0.5, -18.29) * mm});
            skLineSegment(sketch, "E20.0.1.142", {"start": v(-29.97, -15.75) * mm, "end": v(-29.97, -24.9) * mm});
            skPoint(sketch, "E20.0.1.143", {"position": v(-9.65, -20.32) * mm});
            skPoint(sketch, "E20.0.1.144", {"position": v(9.65, -18.29) * mm});
            skLineSegment(sketch, "E20.0.1.145", {"start": v(0.5, -24.9) * mm, "end": v(9.65, -24.9) * mm});
            skPoint(sketch, "E20.0.1.146", {"position": v(9.65, -22.35) * mm});
            skPoint(sketch, "E20.0.1.147", {"position": v(-0.5, -8.13) * mm});
            skPoint(sketch, "E20.0.1.148", {"position": v(-0.5, -12.2) * mm});
            skLineSegment(sketch, "E20.0.1.149", {"start": v(-19.81, -21.84) * mm, "end": v(-19.81, -22.86) * mm});
            skLineSegment(sketch, "E20.0.1.150", {"start": v(-19.81, -14.73) * mm, "end": v(-18.8, -14.73) * mm});
            skLineSegment(sketch, "E20.0.1.151", {"start": v(10.67, -11.68) * mm, "end": v(10.67, -12.7) * mm});
            skLineSegment(sketch, "E20.0.1.152", {"start": v(-15.75, -14.73) * mm, "end": v(-14.73, -14.73) * mm});
            skLineSegment(sketch, "E20.0.1.153", {"start": v(19.81, -5.59) * mm, "end": v(19.81, -6.6) * mm});
            skLineSegment(sketch, "E20.0.1.154", {"start": v(29.97, -17.78) * mm, "end": v(29.97, -18.8) * mm});
            skLineSegment(sketch, "E20.0.1.155", {"start": v(-9.65, -9.65) * mm, "end": v(-9.65, -10.67) * mm});
            skLineSegment(sketch, "E20.0.1.156", {"start": v(-1.52, -24.9) * mm, "end": v(-0.5, -24.9) * mm});
            skLineSegment(sketch, "E20.0.1.157", {"start": v(0.5, -21.84) * mm, "end": v(0.5, -22.86) * mm});
            skLineSegment(sketch, "E20.0.1.158", {"start": v(-21.84, -24.9) * mm, "end": v(-20.83, -24.9) * mm});
            skLineSegment(sketch, "E20.0.1.159", {"start": v(-23.88, -24.9) * mm, "end": v(-22.86, -24.9) * mm});
            skLineSegment(sketch, "E20.0.1.160", {"start": v(0.5, -14.73) * mm, "end": v(2.54, -14.73) * mm, "construction": true});
            skLineSegment(sketch, "E20.0.1.161", {"start": v(-1.52, -15.75) * mm, "end": v(-0.5, -15.75) * mm});
            skLineSegment(sketch, "E20.0.1.162", {"start": v(0.5, -5.59) * mm, "end": v(1.52, -5.59) * mm});
            skLineSegment(sketch, "E20.0.1.163", {"start": v(16.76, -15.75) * mm, "end": v(17.78, -15.75) * mm});
            skLineSegment(sketch, "E20.0.1.164", {"start": v(12.7, -24.9) * mm, "end": v(13.72, -24.9) * mm});
            skLineSegment(sketch, "E20.0.1.165", {"start": v(18.8, -24.9) * mm, "end": v(19.81, -24.9) * mm});
            skLineSegment(sketch, "E20.0.1.166", {"start": v(-27.94, -24.9) * mm, "end": v(-26.92, -24.9) * mm});
            skLineSegment(sketch, "E20.0.1.167", {"start": v(-13.72, -5.59) * mm, "end": v(-12.7, -5.59) * mm});
            skLineSegment(sketch, "E20.0.1.168", {"start": v(-20.83, -7.62) * mm, "end": v(-20.83, -8.64) * mm});
            skLineSegment(sketch, "E20.0.1.169", {"start": v(-29.97, -5.59) * mm, "end": v(-29.97, -6.6) * mm});
            skLineSegment(sketch, "E20.0.1.170", {"start": v(-20.83, -11.68) * mm, "end": v(-20.83, -12.7) * mm});
            skLineSegment(sketch, "E20.0.1.171", {"start": v(-29.97, -9.65) * mm, "end": v(-29.97, -10.67) * mm});
            skLineSegment(sketch, "E20.0.1.172", {"start": v(-29.97, -15.75) * mm, "end": v(-28.96, -15.75) * mm});
            skLineSegment(sketch, "E20.0.1.173", {"start": v(22.86, -5.59) * mm, "end": v(23.88, -5.59) * mm});
            skLineSegment(sketch, "E20.0.1.174", {"start": v(10.67, -24.9) * mm, "end": v(11.68, -24.9) * mm});
            skLineSegment(sketch, "E20.0.1.175", {"start": v(8.64, -5.59) * mm, "end": v(9.65, -5.59) * mm});
            skLineSegment(sketch, "E20.0.1.176", {"start": v(0.5, -14.73) * mm, "end": v(1.52, -14.73) * mm});
            skLineSegment(sketch, "E20.0.1.177", {"start": v(29.97, -15.75) * mm, "end": v(29.97, -16.76) * mm});
            skLineSegment(sketch, "E20.0.1.178", {"start": v(12.7, -15.75) * mm, "end": v(13.72, -15.75) * mm});
            skLineSegment(sketch, "E20.0.1.179", {"start": v(28.96, -14.73) * mm, "end": v(29.97, -14.73) * mm});
            skLineSegment(sketch, "E20.0.1.180", {"start": v(19.81, -13.72) * mm, "end": v(19.81, -14.73) * mm});
            skLineSegment(sketch, "E20.0.1.181", {"start": v(-19.81, -19.81) * mm, "end": v(-19.81, -20.83) * mm});
            skLineSegment(sketch, "E20.0.1.182", {"start": v(-17.78, -14.73) * mm, "end": v(-16.76, -14.73) * mm});
            skLineSegment(sketch, "E20.0.1.183", {"start": v(-29.97, -13.72) * mm, "end": v(-29.97, -14.73) * mm});
            skLineSegment(sketch, "E20.0.1.184", {"start": v(0.5, -19.81) * mm, "end": v(0.5, -20.83) * mm});
            skLineSegment(sketch, "E20.0.1.185", {"start": v(29.97, -19.81) * mm, "end": v(29.97, -20.83) * mm});
            skLineSegment(sketch, "E20.0.1.186", {"start": v(20.83, -5.59) * mm, "end": v(21.84, -5.59) * mm});
            skLineSegment(sketch, "E20.0.1.187", {"start": v(26.92, -5.59) * mm, "end": v(27.94, -5.59) * mm});
            skLineSegment(sketch, "E20.0.1.188", {"start": v(-27.94, -15.75) * mm, "end": v(-26.92, -15.75) * mm});
            skLineSegment(sketch, "E20.0.1.189", {"start": v(-29.97, -24.9) * mm, "end": v(-27.94, -24.9) * mm, "construction": true});
            skLineSegment(sketch, "E20.0.1.190", {"start": v(-20.83, -9.65) * mm, "end": v(-20.83, -10.67) * mm});
            skLineSegment(sketch, "E20.0.1.191", {"start": v(-25.9, -15.75) * mm, "end": v(-24.9, -15.75) * mm});
            skLineSegment(sketch, "E20.0.1.192", {"start": v(-29.97, -24.9) * mm, "end": v(-28.96, -24.9) * mm});
            skLineSegment(sketch, "E20.0.1.193", {"start": v(20.83, -14.73) * mm, "end": v(22.86, -14.73) * mm, "construction": true});
            skLineSegment(sketch, "E20.0.1.194", {"start": v(-17.78, -5.59) * mm, "end": v(-16.76, -5.59) * mm});
            skLineSegment(sketch, "E20.0.1.195", {"start": v(-11.68, -5.59) * mm, "end": v(-10.67, -5.59) * mm});
            skLineSegment(sketch, "E20.0.1.196", {"start": v(20.83, -15.75) * mm, "end": v(20.83, -16.76) * mm});
            skLineSegment(sketch, "E20.0.1.197", {"start": v(14.73, -15.75) * mm, "end": v(15.75, -15.75) * mm});
            skLineSegment(sketch, "E20.0.1.198", {"start": v(14.73, -24.9) * mm, "end": v(15.75, -24.9) * mm});
            skLineSegment(sketch, "E20.0.1.199", {"start": v(10.67, -13.72) * mm, "end": v(10.67, -14.73) * mm});
            skLineSegment(sketch, "E20.0.1.200", {"start": v(8.64, -14.73) * mm, "end": v(9.65, -14.73) * mm});
            skLineSegment(sketch, "E20.0.1.201", {"start": v(2.54, -14.73) * mm, "end": v(3.56, -14.73) * mm});
            skLineSegment(sketch, "E20.0.1.202", {"start": v(-9.65, -24.9) * mm, "end": v(-7.62, -24.9) * mm, "construction": true});
            skLineSegment(sketch, "E20.0.1.203", {"start": v(20.83, -23.88) * mm, "end": v(20.83, -24.9) * mm});
            skLineSegment(sketch, "E20.0.1.204", {"start": v(10.67, -15.75) * mm, "end": v(11.68, -15.75) * mm});
            skLineSegment(sketch, "E20.0.1.205", {"start": v(26.92, -14.73) * mm, "end": v(27.94, -14.73) * mm});
            skLineSegment(sketch, "E20.0.1.206", {"start": v(2.54, -5.59) * mm, "end": v(3.56, -5.59) * mm});
            skLineSegment(sketch, "E20.0.1.207", {"start": v(-15.75, -5.59) * mm, "end": v(-14.73, -5.59) * mm});
            skLineSegment(sketch, "E20.0.1.208", {"start": v(19.81, -11.68) * mm, "end": v(19.81, -12.7) * mm});
            skLineSegment(sketch, "E20.0.1.209", {"start": v(10.67, -5.59) * mm, "end": v(10.67, -6.6) * mm});
            skLineSegment(sketch, "E20.0.1.210", {"start": v(-19.81, -15.75) * mm, "end": v(-19.81, -16.76) * mm});
            skLineSegment(sketch, "E20.0.1.211", {"start": v(-10.67, -15.75) * mm, "end": v(-10.67, -16.76) * mm});
            skLineSegment(sketch, "E20.0.1.212", {"start": v(-23.88, -15.75) * mm, "end": v(-22.86, -15.75) * mm});
            skLineSegment(sketch, "E20.0.1.213", {"start": v(4.57, -5.59) * mm, "end": v(5.59, -5.59) * mm});
            skLineSegment(sketch, "E20.0.1.214", {"start": v(19.81, -7.62) * mm, "end": v(19.81, -8.64) * mm});
            skLineSegment(sketch, "E20.0.1.215", {"start": v(20.83, -21.84) * mm, "end": v(20.83, -22.86) * mm});
            skLineSegment(sketch, "E20.0.1.216", {"start": v(-19.81, -23.88) * mm, "end": v(-19.81, -24.9) * mm});
            skLineSegment(sketch, "E20.0.1.217", {"start": v(-10.67, -23.88) * mm, "end": v(-10.67, -24.9) * mm});
            skLineSegment(sketch, "E20.0.1.218", {"start": v(-19.81, -17.78) * mm, "end": v(-19.81, -18.8) * mm});
            skLineSegment(sketch, "E20.0.1.219", {"start": v(-9.65, -11.68) * mm, "end": v(-9.65, -12.7) * mm});
            skLineSegment(sketch, "E20.0.1.220", {"start": v(0.5, -23.88) * mm, "end": v(0.5, -24.9) * mm});
            skLineSegment(sketch, "E20.0.1.221", {"start": v(0.5, -15.75) * mm, "end": v(0.5, -16.76) * mm});
            skLineSegment(sketch, "E20.0.1.222", {"start": v(28.96, -5.59) * mm, "end": v(29.97, -5.59) * mm});
            skLineSegment(sketch, "E20.0.1.223", {"start": v(24.9, -14.73) * mm, "end": v(25.9, -14.73) * mm});
            skLineSegment(sketch, "E20.0.1.224", {"start": v(-29.97, -11.68) * mm, "end": v(-29.97, -12.7) * mm});
            skLineSegment(sketch, "E20.0.1.225", {"start": v(-19.81, -14.73) * mm, "end": v(-17.78, -14.73) * mm, "construction": true});
            skLineSegment(sketch, "E20.0.1.226", {"start": v(9.65, -23.88) * mm, "end": v(9.65, -24.9) * mm});
            skLineSegment(sketch, "E20.0.1.227", {"start": v(9.65, -15.75) * mm, "end": v(9.65, -16.76) * mm});
            skLineSegment(sketch, "E20.0.1.228", {"start": v(20.83, -14.73) * mm, "end": v(21.84, -14.73) * mm});
            skLineSegment(sketch, "E20.0.1.229", {"start": v(22.86, -14.73) * mm, "end": v(23.88, -14.73) * mm});
            skLineSegment(sketch, "E20.0.1.230", {"start": v(-21.84, -15.75) * mm, "end": v(-20.83, -15.75) * mm});
            skLineSegment(sketch, "E20.0.1.231", {"start": v(16.76, -24.9) * mm, "end": v(17.78, -24.9) * mm});
            skLineSegment(sketch, "E20.0.1.232", {"start": v(10.67, -7.62) * mm, "end": v(10.67, -8.64) * mm});
            skLineSegment(sketch, "E20.0.1.233", {"start": v(-20.83, -5.59) * mm, "end": v(-20.83, -6.6) * mm});
            skLineSegment(sketch, "E20.0.1.234", {"start": v(-10.67, -19.81) * mm, "end": v(-10.67, -20.83) * mm});
            skLineSegment(sketch, "E20.0.1.235", {"start": v(6.6, -5.59) * mm, "end": v(7.62, -5.59) * mm});
            skLineSegment(sketch, "E20.0.1.236", {"start": v(20.83, -19.81) * mm, "end": v(20.83, -20.83) * mm});
            skLineSegment(sketch, "E20.0.1.237", {"start": v(10.67, -9.65) * mm, "end": v(10.67, -10.67) * mm});
            skLineSegment(sketch, "E20.0.1.238", {"start": v(20.83, -17.78) * mm, "end": v(20.83, -18.8) * mm});
            skLineSegment(sketch, "E20.0.1.239", {"start": v(-20.83, -13.72) * mm, "end": v(-20.83, -14.73) * mm});
            skLineSegment(sketch, "E20.0.1.240", {"start": v(-11.68, -14.73) * mm, "end": v(-10.67, -14.73) * mm});
            skLineSegment(sketch, "E20.0.1.241", {"start": v(-9.65, -13.72) * mm, "end": v(-9.65, -14.73) * mm});
            skLineSegment(sketch, "E20.0.1.242", {"start": v(-9.65, -5.59) * mm, "end": v(-9.65, -6.6) * mm});
            skLineSegment(sketch, "E20.0.1.243", {"start": v(24.9, -5.59) * mm, "end": v(25.9, -5.59) * mm});
            skLineSegment(sketch, "E20.0.1.244", {"start": v(18.8, -15.75) * mm, "end": v(19.81, -15.75) * mm});
            skLineSegment(sketch, "E20.0.1.245", {"start": v(-19.81, -24.9) * mm, "end": v(-10.67, -24.9) * mm});
            skLineSegment(sketch, "E20.0.1.246", {"start": v(19.81, -9.65) * mm, "end": v(19.81, -10.67) * mm});
            skLineSegment(sketch, "E20.0.1.247", {"start": v(-13.72, -14.73) * mm, "end": v(-12.7, -14.73) * mm});
            skLineSegment(sketch, "E20.0.1.248", {"start": v(-25.9, -24.9) * mm, "end": v(-24.9, -24.9) * mm});
            skLineSegment(sketch, "E20.0.1.249", {"start": v(6.6, -14.73) * mm, "end": v(7.62, -14.73) * mm});
            skLineSegment(sketch, "E20.0.1.250", {"start": v(-0.5, -13.72) * mm, "end": v(-0.5, -14.73) * mm});
            skLineSegment(sketch, "E20.0.1.251", {"start": v(-0.5, -5.59) * mm, "end": v(-0.5, -6.6) * mm});
            skLineSegment(sketch, "E20.0.1.252", {"start": v(29.97, -23.88) * mm, "end": v(29.97, -24.9) * mm});
            skLineSegment(sketch, "E20.0.1.253", {"start": v(10.67, -24.9) * mm, "end": v(12.7, -24.9) * mm, "construction": true});
            skLineSegment(sketch, "E20.0.1.254", {"start": v(29.97, -21.84) * mm, "end": v(29.97, -22.86) * mm});
            skLineSegment(sketch, "E20.0.1.255", {"start": v(-19.81, -5.59) * mm, "end": v(-18.8, -5.59) * mm});
            skLineSegment(sketch, "E20.0.1.256", {"start": v(-29.97, -7.62) * mm, "end": v(-29.97, -8.64) * mm});
            skLineSegment(sketch, "E20.0.1.257", {"start": v(-3.56, -24.9) * mm, "end": v(-2.54, -24.9) * mm});
            skLineSegment(sketch, "E20.0.1.258", {"start": v(-9.65, -15.75) * mm, "end": v(-8.64, -15.75) * mm});
            skLineSegment(sketch, "E20.0.1.259", {"start": v(-9.65, -24.9) * mm, "end": v(-8.64, -24.9) * mm});
            skLineSegment(sketch, "E20.0.1.260", {"start": v(-7.62, -15.75) * mm, "end": v(-6.6, -15.75) * mm});
            skLineSegment(sketch, "E20.0.1.261", {"start": v(-7.62, -24.9) * mm, "end": v(-6.6, -24.9) * mm});
            skLineSegment(sketch, "E20.0.1.262", {"start": v(-5.59, -24.9) * mm, "end": v(-4.57, -24.9) * mm});
            skLineSegment(sketch, "E20.0.1.263", {"start": v(9.65, -19.81) * mm, "end": v(9.65, -20.83) * mm});
            skLineSegment(sketch, "E20.0.1.264", {"start": v(-9.65, -7.62) * mm, "end": v(-9.65, -8.64) * mm});
            skLineSegment(sketch, "E20.0.1.265", {"start": v(-10.67, -21.84) * mm, "end": v(-10.67, -22.86) * mm});
            skLineSegment(sketch, "E20.0.1.266", {"start": v(-0.5, -7.62) * mm, "end": v(-0.5, -8.64) * mm});
            skLineSegment(sketch, "E20.0.1.267", {"start": v(-0.5, -9.65) * mm, "end": v(-0.5, -10.67) * mm});
            skLineSegment(sketch, "E20.0.1.268", {"start": v(9.65, -21.84) * mm, "end": v(9.65, -22.86) * mm});
            skLineSegment(sketch, "E20.0.1.269", {"start": v(4.57, -14.73) * mm, "end": v(5.59, -14.73) * mm});
            skLineSegment(sketch, "E20.0.1.270", {"start": v(-0.5, -11.68) * mm, "end": v(-0.5, -12.7) * mm});
            skLineSegment(sketch, "E20.0.1.271", {"start": v(-10.67, -17.78) * mm, "end": v(-10.67, -18.8) * mm});
            skLineSegment(sketch, "E20.0.1.272", {"start": v(0.5, -17.78) * mm, "end": v(0.5, -18.8) * mm});
            skLineSegment(sketch, "E20.0.1.273", {"start": v(9.65, -17.78) * mm, "end": v(9.65, -18.8) * mm});
            skLineSegment(sketch, "E20.0.1.274", {"start": v(-3.56, -15.75) * mm, "end": v(-2.54, -15.75) * mm});
            skLineSegment(sketch, "E20.0.1.275", {"start": v(-5.59, -15.75) * mm, "end": v(-4.57, -15.75) * mm});
            skLineSegment(sketch, "E20.direction2", {"start": v(-29.97, -4.57) * mm, "end": v(-29.97, -24.9) * mm, "construction": true});
            skSolve(sketch);
        }
        {
            var Q0;
            Q0 = qSketchRegion(id + "F2", true);
            extrude(context, id + "F3", {"entities" : qUnion([Q0]), "operationType" : NewBodyOperationType.ADD, "depth" : .6 * mm});
        }
        {
            var Q0;
            Q0=makeQuery(id+"F1.opExtrude","CAP_FACE",FACE,{"disambiguationData":[OSD([sQuery(id+"F0.wireOp",EDGE,"E0")])],"isStart":true});
            var sketch = newSketch(context, id + "F4", { "sketchPlane" : qUnion([Q0])});
            skCircle(sketch, "E21", {"center": v(0, 0) * mm, "radius": 27.94 * mm});
            skCircle(sketch, "E22", {"center": v(0, 0) * mm, "radius": 47.3 * mm});
            skPoint(sketch, "E23", {"position": v(0, -27.94) * mm});
            skSolve(sketch);
        }
        {
            var Q0;
            Q0 = qSketchRegion(id + "F4", true);
            extrude(context, id + "F5", {"entities" : qUnion([Q0]), "operationType" : NewBodyOperationType.REMOVE, "oppositeDirection" : true, "depth" : 25.4 * mm});
        }
        {
            var Q0;
            Q0 = qSketchRegion(id + "F0", true);
            extrude(context, id + "F6", {"entities" : qUnion([Q0]), "depth" : 5 * mm});
        }
        {
            var Q0;
            Q0=makeQuery(id+"F6.opExtrude","CAP_FACE",FACE,{"disambiguationData":[OSD([sQuery(id+"F0.wireOp",EDGE,"E0")])],"isStart":false});
            var sketch = newSketch(context, id + "F7", { "sketchPlane" : qUnion([Q0])});
            skCircle(sketch, "E24", {"center": v(0, 0) * mm, "radius": 27.94 * mm});
            skCircle(sketch, "E25", {"center": v(0, 0) * mm, "radius": 25.9 * mm});
            skSolve(sketch);
        }
        {
            var Q0;
            Q0 = qSketchRegion(id + "F7", true);
            extrude(context, id + "F8", {"entities" : qUnion([Q0]), "operationType" : NewBodyOperationType.REMOVE, "depth" : 25.4 * mm});
        }
        {
            var Q0;
            Q0=makeQuery(id+"F6.opExtrude","CAP_FACE",FACE,{"disambiguationData":[OSD([sQuery(id+"F0.wireOp",EDGE,"E0")])],"isStart":false});
            var sketch = newSketch(context, id + "F9", { "sketchPlane" : qUnion([Q0])});
            skLineSegment(sketch, "E26.bottom", {"start": v(-20.02, 15.03) * mm, "end": v(20.03, 15.03) * mm});
            skLineSegment(sketch, "E26.top", {"start": v(-20.02, 9.1) * mm, "end": v(20.03, 9.1) * mm});
            skLineSegment(sketch, "E26.left", {"start": v(-20.02, 15.03) * mm, "end": v(-20.02, 9.1) * mm});
            skLineSegment(sketch, "E26.right", {"start": v(20.03, 15.03) * mm, "end": v(20.03, 9.1) * mm});
            skSolve(sketch);
        }
        {
            var Q0;
            Q0 = qSketchRegion(id + "F9", true);
            extrude(context, id + "F10", {"entities" : qUnion([Q0]), "operationType" : NewBodyOperationType.REMOVE, "depth" : 25.4 * mm});
        }
        {
            var Q0;
            Q0=makeQuery(id+"F6.opExtrude","CAP_FACE",FACE,{"disambiguationData":[OSD([sQuery(id+"F0.wireOp",EDGE,"E0")])],"isStart":false});
            var sketch = newSketch(context, id + "F11", { "sketchPlane" : qUnion([Q0])});
            skText(sketch, "E27", { "text": "BURDEN IRON CO", "fontName": "OpenSans-Regular.ttf"});
            skLineSegment(sketch, "E28", {"start": v(0, 0) * mm, "end": v(0, 20.1) * mm, "construction": true});
            const initialGuessF11  = {"E27": [-0.01905, 0.01041, 1, 0, 0.00327]};
            skSetInitialGuess(sketch, initialGuessF11);
            skSolve(sketch);
        }
        {
            var Q0;
            Q0 = qSketchRegion(id + "F11", true);
            extrude(context, id + "F12", {"entities" : qUnion([Q0]), "operationType" : NewBodyOperationType.ADD, "depth" : 1 * mm, "hasSecondDirection" : true, "secondDirectionOppositeDirection" : true, "secondDirectionDepth" : 1 * mm});
        }
        {
            var Q0;
            Q0=makeQuery(id+"F8.boolean.opBoolean","COPY",FACE,{"derivedFrom":makeQuery(id+"F8.opExtrude","CAP_FACE",FACE,{"disambiguationData":[OSD([sQuery(id+"F7.wireOp",EDGE,"E24"),sQuery(id+"F7.wireOp",EDGE,"E25")])],"isStart":true})});
            var sketch = newSketch(context, id + "F13", { "sketchPlane" : qUnion([Q0])});
            skLineSegment(sketch, "E29.bottom", {"start": v(-20.16, -14.98) * mm, "end": v(20.18, -14.98) * mm});
            skLineSegment(sketch, "E29.top", {"start": v(-20.16, -9.02) * mm, "end": v(20.18, -9.02) * mm});
            skLineSegment(sketch, "E29.left", {"start": v(-20.16, -14.98) * mm, "end": v(-20.16, -9.02) * mm});
            skLineSegment(sketch, "E29.right", {"start": v(20.18, -14.98) * mm, "end": v(20.18, -9.02) * mm});
            skSolve(sketch);
        }
        {
            var Q0;
            Q0 = qSketchRegion(id + "F13", true);
            extrude(context, id + "F14", {"entities" : qUnion([Q0]), "operationType" : NewBodyOperationType.REMOVE, "depth" : 25.4 * mm});
        }
        {
            var Q0;
            Q0=makeQuery(id+"F14.boolean.opBoolean","COPY",FACE,{"derivedFrom":makeQuery(id+"F14.opExtrude","CAP_FACE",FACE,{"disambiguationData":[OSD([sQuery(id+"F13.wireOp",EDGE,"E29.bottom"),sQuery(id+"F13.wireOp",EDGE,"E29.top"),sQuery(id+"F13.wireOp",EDGE,"E29.left"),sQuery(id+"F13.wireOp",EDGE,"E29.right")])],"isStart":true})});
            var sketch = newSketch(context, id + "F15", { "sketchPlane" : qUnion([Q0])});
            skText(sketch, "E30", { "text": "TROY  NY", "fontName": "OpenSans-Bold.ttf"});
            skLineSegment(sketch, "E31", {"start": v(0, 0) * mm, "end": v(0, -17.15) * mm, "construction": true});
            const initialGuessF15  = {"E30": [-0.01614, -0.01474, 1, 0, 0.00496]};
            skSetInitialGuess(sketch, initialGuessF15);
            skSolve(sketch);
        }
        {
            var Q0;
            Q0 = qSketchRegion(id + "F15", true);
            extrude(context, id + "F16", {"entities" : qUnion([Q0]), "operationType" : NewBodyOperationType.ADD, "depth" : 1 * mm});
        }
    });
